FCSTD DOCUMENT  (FreeCAD 0.20R29410 (Git))
Label: SoLoNodesMay31_2023
License: All rights reserved
LicenseURL: http://en.wikipedia.org/wiki/All_rights_reserved
objects: Part::Feature×153, Sketcher::SketchObject×60, Part::Cylinder×60, Part::MultiFuse×52, Part::Cut×25, Part::Fillet×23, Part::Extrusion×20, Part::Loft×20, App::Part×19, Part::Sphere×6, Mesh::Feature×4, Part::Box×3, Part::Compound×2, Part::Cone×1
note: 425 computed .brp shape members not serialized (recipe doc carries the construction recipe); baked Part::Feature solids carry a one-line shape summary decoded from their .brp

FEATURE [Part::Feature] Part__Feature  label="PH Pan head screw M2x0.40 x 6"
  Placement = pos=(101.945,-83.8381,-1.82512) rot=(0,0,1;3.14159rad)
  shape: bbox 4.006 x 4.006 x 7.57 mm, 32 faces (baked)
FEATURE [Part::Feature] Part__Feature001  label="Part 8"
  Placement = pos=(178.445,24.1619,-39.4251) rot=(0,1,0;3.14159rad)
  shape: bbox 166 x 27.4 x 2 mm, 14 faces (baked)
FEATURE [Part::Feature] Part__Feature002  label="event gore PMF100320"
  Placement = pos=(79.1369,-76.58,11.5741) rot=(0,-1,0;0.037482rad)
  shape: bbox 2.468 x 15.31 x 15.29 mm, 4 faces (baked)
FEATURE [Part::Feature] Part__Feature003  label="event gore PMF100321"
  Placement = pos=(79.1369,-76.58,11.5741) rot=(0,-1,0;0.037482rad)
  shape: bbox 15.95 x 18.27 x 18.26 mm, 114 faces (baked)
FEATURE [Part::Feature] Part__Feature004  label="PH Pan head screw M2x0.40 x 007"
  Placement = pos=(101.945,24.1619,-1.82512) rot=(0,0,1;0rad)
  shape: bbox 4.006 x 4.006 x 7.57 mm, 32 faces (baked)
FEATURE [Part::Feature] Part__Feature005  label="WPB20-28-7_3D"
  Placement = pos=(178.445,24.1619,30.5749) rot=(0,0,1;0rad)
  shape: bbox 200.6 x 280.6 x 46.01 mm, 1035 faces (baked)
FEATURE [Part::Feature] Part__Feature006  label="PH Pan head screw M2x0.40 x 008"
  Placement = pos=(254.945,-83.8381,-1.82512) rot=(0,0,1;3.14159rad)
  shape: bbox 4.006 x 4.006 x 7.57 mm, 32 faces (baked)
FEATURE [Part::Feature] Part__Feature007  label="Cable Gland PG7-PG19 Lock Nut_PG13.5"
  Placement = pos=(223.445,-112.627,11.6686) rot=(1,0,0;0.037482rad)
  shape: bbox 29.02 x 6.449 x 29 mm, 29 faces (baked)
FEATURE [Part::Feature] Part__Feature008  label="Cable Gland PG7-PG19 Body_PG13.5"
  Placement = pos=(223.445,-118.923,11.4325) rot=(0,-0.01874,0.999824;3.14159rad)
  shape: bbox 25.06 x 36.36 x 23.18 mm, 156 faces (baked)
FEATURE [Part::Feature] Part__Feature009  label="Cable Gland PG7-PG19 Washer_PG13.5"
  Placement = pos=(223.445,-115.725,11.5524) rot=(0,-0.01874,0.999824;3.14159rad)
  shape: bbox 25 x 2.136 x 25.03 mm, 4 faces (baked)
FEATURE [Part::Feature] Part__Feature010  label="Cable Gland PG7-PG19 Gland Nut_PG13.5"
  Placement = pos=(223.445,-132.014,10.9416) rot=(0.825324,-0.010582,0.56456;3.17253rad)
  shape: bbox 25.82 x 20.19 x 25.8 mm, 50 faces (baked)
FEATURE [Part::Feature] Part__Feature011  label="Cable Gland PG7-PG19 Sleeve_PG13.5"
  Placement = pos=(223.445,-137.51,10.7355) rot=(0,-0.01874,0.999824;3.14159rad)
  shape: bbox 15.7 x 8.583 x 15.99 mm, 4 faces (baked)
FEATURE [App::Part] Cable_Gland_PG7_PG19__PG13_5__1_  label="Cable Gland PG7-PG19, PG13.5 <1>"
  Group = -> [Part__Feature007,Part__Feature008,Part__Feature009,Part__Feature010,Part__Feature011]
  Origin = -> Origin
FEATURE [Part::Feature] Part__Feature012  label="WPMB-M4-2"
  Placement = pos=(178.445,24.1619,-13.4251) rot=(0,1,0;3.14159rad)
  shape: bbox 91.99 x 91.99 x 12.05 mm, 899 faces (baked)
FEATURE [Part::Feature] Part__Feature013  label="Micro_USB_Plug v10"
  Placement = pos=(255.557,33.7719,7.31475) rot=(0.577351,0.577352,-0.577348;4.18879rad)
  shape: bbox 4.78 x 0.2 x 0.4672 mm, 14 faces (baked)
FEATURE [Part::Feature] Part__Feature014  label="Micro_USB_Plug_Connector"
  Placement = pos=(255.557,33.7719,7.31475) rot=(0.577351,0.577352,-0.577348;4.18879rad)
  shape: bbox 7.5 x 6.85 x 1.85 mm, 68 faces (baked)
FEATURE [Part::Feature] Part__Feature015  label="Micro_USB_Plug v011"
  Placement = pos=(255.557,33.7719,7.31475) rot=(0.577351,0.577352,-0.577348;4.18879rad)
  shape: bbox 4.78 x 0.2 x 0.4672 mm, 14 faces (baked)
FEATURE [Part::Feature] Part__Feature016  label="Micro_USB_Plug_Connector001"
  Placement = pos=(255.557,33.7719,7.31475) rot=(0.577351,0.577352,-0.577348;4.18879rad)
  shape: bbox 4.574 x 0.32 x 1.625 mm, 11 faces (baked)
FEATURE [Part::Feature] Part__Feature017  label="micro_usb_plug rt angle"
  Placement = pos=(255.557,33.7719,7.31475) rot=(0.577351,0.577352,-0.577348;4.18879rad)
  shape: bbox 12.25 x 19.75 x 7.006 mm, 151 faces (baked)
FEATURE [Part::Feature] Part__Feature018  label="Micro_USB_Plug v012"
  Placement = pos=(255.557,33.7719,7.31475) rot=(0.577351,0.577352,-0.577348;4.18879rad)
  shape: bbox 4.78 x 0.2 x 0.4672 mm, 14 faces (baked)
FEATURE [Part::Feature] Part__Feature019  label="Micro_USB_Plug v013"
  Placement = pos=(255.557,33.7719,7.31475) rot=(0.577351,0.577352,-0.577348;4.18879rad)
  shape: bbox 4.78 x 0.2 x 0.4672 mm, 14 faces (baked)
FEATURE [Part::Feature] Part__Feature020  label="Wire"
  Placement = pos=(255.557,33.7719,7.31475) rot=(0.577351,0.577352,-0.577348;4.18879rad)
  shape: bbox 3.2 x 9.5 x 3.2 mm, 3 faces (baked)
FEATURE [Part::Feature] Part__Feature021  label="Micro_USB_Plug_Connector002"
  Placement = pos=(255.557,33.7719,7.31475) rot=(0.577351,0.577352,-0.577348;4.18879rad)
  shape: bbox 4.7 x 0.32 x 1.625 mm, 11 faces (baked)
FEATURE [Part::Feature] Part__Feature022  label="Micro_USB_Plug v014"
  Placement = pos=(255.557,33.7719,7.31475) rot=(0.577351,0.577352,-0.577348;4.18879rad)
  shape: bbox 4.78 x 0.2 x 0.4672 mm, 14 faces (baked)
FEATURE [Part::Feature] Part__Feature023  label="Micro_USB_Plug_Connector003"
  Placement = pos=(255.557,33.7719,7.31475) rot=(0.577351,0.577352,-0.577348;4.18879rad)
  shape: bbox 7.5 x 6.35 x 1.35 mm, 54 faces (baked)
FEATURE [Part::Feature] Part__Feature024  label="2_C_3_4_6_1_1"
  Placement = pos=(205.099,-19.2281,8.57488) rot=(-1,-3e-06,-3e-06;1.57079rad)
  shape: bbox 73.52 x 148.2 x 33.63 mm, 876 faces (baked)
FEATURE [Part::Feature] Part__Feature025  label="2_BAT_3_4_6_1_1"
  Placement = pos=(205.099,-19.2281,8.57488) rot=(-1,-3e-06,-3e-06;1.57079rad)
  shape: bbox 14.36 x 15.32 x 64.97 mm, 83 faces (baked)
FEATURE [Part::Feature] Part__Feature026  label="2_B_3_4_6_1_1"
  Placement = pos=(205.099,-19.2281,8.57488) rot=(-1,-3e-06,-3e-06;1.57079rad)
  shape: bbox 78.1 x 152 x 64.86 mm, 1086 faces (baked)
FEATURE [Part::Feature] Part__Feature027  label="2_A_3_4_6_2_1"
  Placement = pos=(205.099,-19.2281,8.57488) rot=(-1,-3e-06,-3e-06;1.57079rad)
  shape: bbox 73.51 x 148.2 x 58.23 mm, 268 faces (baked)
FEATURE [App::Part] V75_ASM__1_  label="V75 ASM <1>"
  Group = -> [Part__Feature013,Part__Feature014,Part__Feature015,Part__Feature016,Part__Feature017,Part__Feature018,Part__Feature019,Part__Feature020,Part__Feature021,Part__Feature022,Part__Feature023,Part__Feature024,Part__Feature025,Part__Feature026,Part__Feature027]
  Origin = -> Origin001
  Placement = pos=(6,15.97,20) rot=(0,0,1;0rad)
FEATURE [Part::Feature] Part__Feature028  label="PH Pan head screw M2x0.40 x 009"
  Placement = pos=(254.945,24.1619,-1.82512) rot=(0,0,1;0rad)
  shape: bbox 4.006 x 4.006 x 7.57 mm, 32 faces (baked)
FEATURE [Part::Feature] Part__Feature029  label="Part 009"
  Placement = pos=(178.445,-83.8381,-39.4251) rot=(1,0,0;3.14159rad)
  shape: bbox 166 x 27.4 x 2 mm, 14 faces (baked)
FEATURE [Part::Feature] Part__Feature030  label="WPC20-28_3D"
  Placement = pos=(178.435,24.1794,31.5749) rot=(0,0,1;0rad)
  shape: bbox 201.1 x 281.1 x 21.57 mm, 1217 faces (baked)
FEATURE [Part::Feature] Part__Feature031  label="Cable Gland PG7-PG19 Sleeve_PG9"
  Placement = pos=(133.445,-133.413,10.8891) rot=(0,-0.01874,0.999824;3.14159rad)
  shape: bbox 11 x 8.207 x 11.28 mm, 4 faces (baked)
FEATURE [Part::Feature] Part__Feature032  label="Cable Gland PG7-PG19 Washer_PG9"
  Placement = pos=(133.445,-115.725,11.5524) rot=(0,-0.01874,0.999824;3.14159rad)
  shape: bbox 19.7 x 1.937 x 19.73 mm, 4 faces (baked)
FEATURE [Part::Feature] Part__Feature033  label="Cable Gland PG7-PG19 Lock Nut_PG9"
  Placement = pos=(133.445,-112.627,11.6686) rot=(1,0,0;0.037482rad)
  shape: bbox 24.34 x 6.322 x 24.32 mm, 29 faces (baked)
FEATURE [Part::Feature] Part__Feature034  label="Cable Gland PG7-PG19 Body_PG9"
  Placement = pos=(133.445,-118.823,11.4362) rot=(0,-0.01874,0.999824;3.14159rad)
  shape: bbox 19.4 x 32.49 x 17.68 mm, 129 faces (baked)
FEATURE [Part::Feature] Part__Feature035  label="Cable Gland PG7-PG19 Gland Nut_PG9"
  Placement = pos=(133.445,-130.065,11.0147) rot=(0.825324,-0.010582,0.56456;3.17253rad)
  shape: bbox 20.81 x 16.04 x 20.8 mm, 48 faces (baked)
FEATURE [App::Part] Cable_Gland_PG7_PG19__PG9__1_  label="Cable Gland PG7-PG19, PG9 <1>"
  Group = -> [Part__Feature031,Part__Feature032,Part__Feature033,Part__Feature034,Part__Feature035]
  Origin = -> Origin002
FEATURE [App::Part] E305__20x28x7cm_  label="box"
  Group = -> [Part__Feature,Part__Feature001,Part__Feature002,Part__Feature003,Part__Feature004,Part__Feature005,Part__Feature006,Cable_Gland_PG7_PG19__PG13_5__1_,Part__Feature012,V75_ASM__1_,Part__Feature028,Part__Feature029,Part__Feature030,Cable_Gland_PG7_PG19__PG9__1_]
  Origin = -> Origin003
  Placement = pos=(175.533,-124.11,-130.152) rot=(0,-0.939693,-0.34202;3.14159rad)
FEATURE [Part::Feature] Part__Feature036  label="id2"
  shape: bbox 274 x 229.5 x 2.5 mm, 53 faces (baked)
FEATURE [Part::Feature] Part__Feature037  label="id5"
  shape: bbox 251.2 x 70.58 x 83.44 mm, 48 faces (baked)
FEATURE [Part::Feature] Part__Feature038  label="id8"
  shape: bbox 253.5 x 2.737 x 2.883 mm, 6 faces (baked)
FEATURE [Part::MultiFuse] Fusion  label="solarPanelMount"
  Placement = pos=(0,0,0) rot=(1,0,0;0.698132rad)
  Shapes = -> [Part__Feature036,Part__Feature037,Part__Feature038]
FEATURE [Part::Feature] Part__Feature039  label="Part 2"
  Placement = pos=(-0.595807,44.562,74.9733) rot=(1,0,0;3.14159rad)
  shape: bbox 272 x 434 x 1.1 mm, 24 faces (baked)
FEATURE [Part::Feature] Part__Feature041  label="id16"
  Placement = pos=(-0.595807,44.562,69.8733) rot=(0,0,1;0rad)
  shape: bbox 4 x 8.79 x 2 mm, 10 faces (baked)
FEATURE [Part::Feature] Part__Feature042  label="id21"
  Placement = pos=(-0.595807,44.562,69.8733) rot=(0,0,1;0rad)
  shape: bbox 125 x 42.28 x 0.1 mm, 8 faces (baked)
FEATURE [Part::Feature] Part__Feature043  label="id26"
  Placement = pos=(-0.595807,44.562,69.8733) rot=(0,0,1;0rad)
  shape: bbox 125 x 42.28 x 0.1 mm, 8 faces (baked)
FEATURE [Part::Feature] Part__Feature044  label="id31"
  Placement = pos=(-0.595807,44.562,69.8733) rot=(0,0,1;0rad)
  shape: bbox 4 x 8.79 x 2 mm, 10 faces (baked)
FEATURE [Part::Feature] Part__Feature045  label="id36"
  Placement = pos=(-0.595807,44.562,69.8733) rot=(0,0,1;0rad)
  shape: bbox 125 x 42.28 x 0.1 mm, 8 faces (baked)
FEATURE [Part::Feature] Part__Feature046  label="id41"
  Placement = pos=(-0.595807,44.562,69.8733) rot=(0,0,1;0rad)
  shape: bbox 4 x 4 x 2 mm, 4 faces (baked)
FEATURE [Part::Feature] Part__Feature047  label="id46"
  Placement = pos=(-0.595807,44.562,69.8733) rot=(0,0,1;0rad)
  shape: bbox 4 x 4 x 2 mm, 4 faces (baked)
FEATURE [Part::Feature] Part__Feature048  label="id51"
  Placement = pos=(-0.595807,44.562,69.8733) rot=(0,0,1;0rad)
  shape: bbox 125 x 42.28 x 0.1 mm, 8 faces (baked)
FEATURE [Part::Feature] Part__Feature049  label="id56"
  Placement = pos=(-0.595807,44.562,69.8733) rot=(0,0,1;0rad)
  shape: bbox 125 x 42.28 x 0.1 mm, 8 faces (baked)
FEATURE [Part::Feature] Part__Feature050  label="id61"
  Placement = pos=(-0.595807,44.562,69.8733) rot=(0,0,1;0rad)
  shape: bbox 4 x 4 x 2 mm, 4 faces (baked)
FEATURE [Part::Feature] Part__Feature051  label="id66"
  Placement = pos=(-0.595807,44.562,69.8733) rot=(0,0,1;0rad)
  shape: bbox 125 x 42.28 x 0.1 mm, 8 faces (baked)
FEATURE [Part::Feature] Part__Feature052  label="id71"
  Placement = pos=(-0.595807,44.562,69.8733) rot=(0,0,1;0rad)
  shape: bbox 125 x 40.44 x 0.1 mm, 6 faces (baked)
FEATURE [Part::Feature] Part__Feature053  label="id76"
  Placement = pos=(-0.595807,44.562,69.8733) rot=(0,0,1;0rad)
  shape: bbox 125 x 40.44 x 0.1 mm, 6 faces (baked)
FEATURE [Part::Feature] Part__Feature054  label="id81"
  Placement = pos=(-0.595807,44.562,69.8733) rot=(0,0,1;0rad)
  shape: bbox 125 x 42.28 x 0.1 mm, 8 faces (baked)
FEATURE [Part::Feature] Part__Feature055  label="id86"
  Placement = pos=(-0.595807,44.562,69.8733) rot=(0,0,1;0rad)
  shape: bbox 125 x 42.28 x 0.1 mm, 8 faces (baked)
FEATURE [Part::Feature] Part__Feature056  label="id91"
  Placement = pos=(-0.595807,44.562,69.8733) rot=(0,0,1;0rad)
  shape: bbox 125 x 42.28 x 0.1 mm, 8 faces (baked)
FEATURE [Part::Feature] Part__Feature057  label="id96"
  Placement = pos=(-0.595807,44.562,69.8733) rot=(0,0,1;0rad)
  shape: bbox 272 x 434 x 2 mm, 24 faces (baked)
FEATURE [Part::Feature] Part__Feature058  label="id101"
  Placement = pos=(-0.595807,44.562,69.8733) rot=(0,0,1;0rad)
  shape: bbox 125 x 42.28 x 0.1 mm, 8 faces (baked)
FEATURE [Part::Feature] Part__Feature059  label="id106"
  Placement = pos=(-0.595807,44.562,69.8733) rot=(0,0,1;0rad)
  shape: bbox 125 x 42.28 x 0.1 mm, 8 faces (baked)
FEATURE [Part::Feature] Part__Feature060  label="id111"
  Placement = pos=(-0.595807,44.562,69.8733) rot=(0,0,1;0rad)
  shape: bbox 125 x 42.28 x 0.1 mm, 8 faces (baked)
FEATURE [Part::Feature] Part__Feature061  label="id116"
  Placement = pos=(-0.595807,44.562,69.8733) rot=(0,0,1;0rad)
  shape: bbox 4 x 4 x 2 mm, 4 faces (baked)
FEATURE [Part::Feature] Part__Feature062  label="id121"
  Placement = pos=(-0.595807,44.562,69.8733) rot=(0,0,1;0rad)
  shape: bbox 4 x 4 x 2 mm, 4 faces (baked)
FEATURE [Part::Feature] Part__Feature063  label="id126"
  Placement = pos=(-0.595807,44.562,69.8733) rot=(0,0,1;0rad)
  shape: bbox 125 x 42.28 x 0.1 mm, 8 faces (baked)
FEATURE [Part::Feature] Part__Feature064  label="id131"
  Placement = pos=(-0.595807,44.562,69.8733) rot=(0,0,1;0rad)
  shape: bbox 4 x 4 x 2 mm, 4 faces (baked)
FEATURE [Part::Feature] Part__Feature065  label="id136"
  Placement = pos=(-0.595807,44.562,69.8733) rot=(0,0,1;0rad)
  shape: bbox 125 x 40.44 x 0.1 mm, 6 faces (baked)
FEATURE [Part::Feature] Part__Feature066  label="id141"
  Placement = pos=(-0.595807,44.562,69.8733) rot=(0,0,1;0rad)
  shape: bbox 274 x 436 x 2 mm, 18 faces (baked)
FEATURE [Part::Feature] Part__Feature067  label="id146"
  Placement = pos=(-0.595807,44.562,69.8733) rot=(0,0,1;0rad)
  shape: bbox 125 x 42.28 x 0.1 mm, 8 faces (baked)
FEATURE [Part::Feature] Part__Feature068  label="id151"
  Placement = pos=(-0.595807,44.562,69.8733) rot=(0,0,1;0rad)
  shape: bbox 125 x 42.28 x 0.1 mm, 8 faces (baked)
FEATURE [Part::Feature] Part__Feature069  label="id156"
  Placement = pos=(-0.595807,44.562,69.8733) rot=(0,0,1;0rad)
  shape: bbox 125 x 42.28 x 0.1 mm, 8 faces (baked)
FEATURE [Part::Feature] Part__Feature070  label="id161"
  Placement = pos=(-0.595807,44.562,69.8733) rot=(0,0,1;0rad)
  shape: bbox 125 x 40.44 x 0.1 mm, 6 faces (baked)
FEATURE [Part::Feature] Part__Feature076  label="Part 1"
  Placement = pos=(-0.595807,44.562,74.9733) rot=(1,0,0;3.14159rad)
  shape: bbox 274 x 436 x 1.1 mm, 18 faces (baked)
FEATURE [Part::Feature] Part__Feature077  label="JBox - 30 mm"
  Placement = pos=(-50.5959,-43.7114,69.8733) rot=(0,1,0;3.14159rad)
  shape: bbox 30.01 x 30.09 x 5.866 mm, 175 faces (baked)
FEATURE [App::Part] P120  label="solarPanel"
  Group = -> [Part__Feature039,Part__Feature041,Part__Feature042,Part__Feature043,Part__Feature044,Part__Feature045,Part__Feature046,Part__Feature047,Part__Feature048,Part__Feature049,Part__Feature050,Part__Feature051,Part__Feature052,Part__Feature053,Part__Feature054,Part__Feature055,Part__Feature056,Part__Feature057,Part__Feature058,Part__Feature059,Part__Feature060,Part__Feature061,Part__Feature062,+10 more]
  Origin = -> Origin004
  Placement = pos=(0.6,-120,-180) rot=(1,0,0;0.698132rad)
FEATURE [Part::Feature] Part__Feature078  label="Open CASCADE STEP translator 7.4 2.1.1"
  shape: bbox 8.3 x 1.9 x 1 mm, 10 faces, 0 solids (baked)
FEATURE [Part::Feature] Part__Feature079  label="Open CASCADE STEP translator 7.4 2.1.2"
  shape: bbox 12.5 x 10 x 1.5 mm, 6 faces, 0 solids (baked)
FEATURE [Part::Feature] Part__Feature080  label="Open CASCADE STEP translator 7.4 2.1.3"
  shape: bbox 12.5 x 10 x 1.5 mm, 6 faces, 0 solids (baked)
FEATURE [Part::Feature] Part__Feature081  label="Open CASCADE STEP translator 7.4 2.1.4"
  shape: bbox 12.5 x 10 x 1.5 mm, 6 faces, 0 solids (baked)
FEATURE [Part::Feature] Part__Feature082  label="Open CASCADE STEP translator 7.4 2.1.5"
  shape: bbox 12.5 x 10 x 1.5 mm, 6 faces, 0 solids (baked)
FEATURE [Part::Feature] Part__Feature083  label="Open CASCADE STEP translator 7.4 2.1.6"
  shape: bbox 89.5 x 57.1 x 20.65 mm, 2741 faces, 0 solids (baked)
FEATURE [App::Part] Open_CASCADE_STEP_translator_7_4_2_1  label="Open CASCADE STEP translator 7.4 2.1"
  Group = -> [Part__Feature078,Part__Feature079,Part__Feature080,Part__Feature081,Part__Feature082,Part__Feature083]
  Origin = -> Origin005
FEATURE [Part::Feature] Part__Feature084  label="m312mm"
  Placement = pos=(63.5,-7,61.5) rot=(0,0.707107,0.707107;3.14159rad)
  shape: bbox 6.201 x 15.54 x 6.201 mm, 70 faces (baked)
FEATURE [Part::Feature] Part__Feature085  label="m312mm001"
  Placement = pos=(14.5,-7,61.5) rot=(-1,0,0;1.5708rad)
  shape: bbox 6.201 x 15.54 x 6.201 mm, 70 faces (baked)
FEATURE [Part::MultiFuse] Fusion003
  Shapes = -> [Part__Feature085,Part__Feature084]
FEATURE [Part::Feature] Part__Feature086  label="m312mm002"
  Placement = pos=(14.5,-7,61.5) rot=(-1,0,0;1.5708rad)
  shape: bbox 6.201 x 15.54 x 6.201 mm, 70 faces (baked)
FEATURE [Part::Feature] Part__Feature087  label="m312mm003"
  Placement = pos=(63.5,-7,61.5) rot=(0,0.707107,0.707107;3.14159rad)
  shape: bbox 6.201 x 15.54 x 6.201 mm, 70 faces (baked)
FEATURE [Part::MultiFuse] Fusion004
  Placement = pos=(0,0,-58) rot=(0,0,1;0rad)
  Shapes = -> [Part__Feature086,Part__Feature087]
FEATURE [Part::MultiFuse] Fusion005  label="m3s"
  Placement = pos=(0.1,-1,0) rot=(0,0,1;0rad)
  Shapes = -> [Fusion004,Fusion003]
FEATURE [App::Part] Open_CASCADE_STEP_translator_7_4_2  label="C4"
  Group = -> [Open_CASCADE_STEP_translator_7_4_2_1,Part__Feature084,Part__Feature085,Fusion003,Part__Feature086,Part__Feature087,Fusion004,Fusion005]
  Origin = -> Origin006
  Placement = pos=(-15,-5,-224) rot=(0.57735,-0.57735,0.57735;2.0944rad)
FEATURE [Part::Feature] Part__Feature088  label="MainBoard"
  shape: bbox 50 x 23 x 1.8 mm, 90 faces (baked)
FEATURE [Part::Feature] Part__Feature089  label="USB Type C Port (SMD Type)"
  Placement = pos=(-18.7,0.12,3.4) rot=(0.707107,-0.707107,0;3.14159rad)
  shape: bbox 7.901 x 8.941 x 4.201 mm, 394 faces, 24 solids (baked)
FEATURE [Part::Feature] Part__Feature090  label="LoRaSTM32Chip"
  Placement = pos=(8.97,0,1.8) rot=(0,0,1;0rad)
  shape: bbox 12 x 12 x 2.5 mm, 68 faces (baked)
FEATURE [Part::Feature] Part__Feature091  label="E10_433M_SMA122"
  Placement = pos=(13,-2.15,1.4) rot=(0,0,1;0rad)
  shape: bbox 11.33 x 1.55 x 1.55 mm, 34 faces (baked)
FEATURE [Part::Feature] Part__Feature092  label="E10_433M_SMA123"
  Placement = pos=(13,-2.15,1.4) rot=(0,0,1;0rad)
  shape: bbox 13.33 x 6.493 x 6.493 mm, 59 faces (baked)
FEATURE [Part::Feature] Part__Feature093  label="CP2012"
  Placement = pos=(-8.75,0.13,1.82) rot=(0,0,1;0rad)
  shape: bbox 4 x 4 x 0.7 mm, 6 faces (baked)
FEATURE [Part::Feature] Part__Feature094  label="u.Fl Antenna Connector - 523-A-1JB"
  Placement = pos=(24.2,5.8,1.8) rot=(0,0.707107,0.707107;3.14159rad)
  shape: bbox 3.1 x 3 x 1.25 mm, 82 faces, 5 solids (baked)
FEATURE [Part::Feature] Part__Feature095  label="Top Traces"
  shape: bbox 49.4 x 23 x 0.02 mm, 7906 faces, 207 solids (baked)
FEATURE [App::Part] LoRa_E5_Mini  label="LoRa-E5-Mini"
  Group = -> [Part__Feature088,Part__Feature089,Part__Feature090,Part__Feature091,Part__Feature092,Part__Feature093,Part__Feature094,Part__Feature095]
  Origin = -> Origin007
  Placement = pos=(-44,0,-220) rot=(0.57735,0.57735,-0.57735;2.0944rad)
FEATURE [Part::Feature] Part__Feature096  label="nanoSupport001"
  Placement = pos=(-30,0,-97) rot=(0.57735,-0.57735,0.57735;2.0944rad)
  shape: bbox 56 x 30 x 43 mm, 8 faces (baked)
FEATURE [Sketcher::SketchObject] Sketch
  FullyConstrained = true
  MapMode = 3
  Placement = pos=(178.445,24.1619,-13.4251) rot=(0,0.707107,-0.707107;3.14159rad)
  Support = -> [Part__Feature012]
  sketch-geometry (32):
    g0: LineSegment StartX=99 StartY=265 StartZ=0 EndX=261 EndY=265 EndZ=0
    g1: LineSegment StartX=261 StartY=265 StartZ=0 EndX=261 EndY=40 EndZ=0
    g2: LineSegment StartX=261 StartY=40 StartZ=0 EndX=99 EndY=40 EndZ=0
    g3: LineSegment StartX=99 StartY=40 StartZ=0 EndX=99 EndY=265 EndZ=0
    g4: Circle CenterX=103.5 CenterY=260.4 CenterZ=0 NormalX=0 NormalY=0 NormalZ=1 AngleXU=0 Radius=1.25
    g5: Circle CenterX=256.5 CenterY=260.4 CenterZ=0 NormalX=0 NormalY=0 NormalZ=1 AngleXU=0 Radius=1.25
    g6: Circle CenterX=103.5 CenterY=152.4 CenterZ=0 NormalX=0 NormalY=0 NormalZ=1 AngleXU=0 Radius=1.25
    g7: Circle CenterX=103.5 CenterY=44.4 CenterZ=0 NormalX=0 NormalY=0 NormalZ=1 AngleXU=0 Radius=1.25
    g8: Circle CenterX=256.5 CenterY=44.4 CenterZ=0 NormalX=0 NormalY=0 NormalZ=1 AngleXU=0 Radius=1.25
    g9: Circle CenterX=256.5 CenterY=152.4 CenterZ=0 NormalX=0 NormalY=0 NormalZ=1 AngleXU=0 Radius=1.25
    g10: Circle CenterX=213.46 CenterY=229.1 CenterZ=0 NormalX=0 NormalY=0 NormalZ=1 AngleXU=0 Radius=1.25
    g11: Circle CenterX=231.46 CenterY=229.1 CenterZ=0 NormalX=0 NormalY=0 NormalZ=1 AngleXU=0 Radius=1.25
    g12: Circle CenterX=213.46 CenterY=194.1 CenterZ=0 NormalX=0 NormalY=0 NormalZ=1 AngleXU=0 Radius=1.25
    g13: Circle CenterX=231.46 CenterY=194.1 CenterZ=0 NormalX=0 NormalY=0 NormalZ=1 AngleXU=0 Radius=1.25
    g14: Circle CenterX=245.95 CenterY=207.08 CenterZ=0 NormalX=0 NormalY=0 NormalZ=1 AngleXU=0 Radius=1.625
    g15: Circle CenterX=196.95 CenterY=207.08 CenterZ=0 NormalX=0 NormalY=0 NormalZ=1 AngleXU=0 Radius=1.625
    g16: Circle CenterX=245.95 CenterY=149.08 CenterZ=0 NormalX=0 NormalY=0 NormalZ=1 AngleXU=0 Radius=1.625
    g17: Circle CenterX=196.95 CenterY=149.08 CenterZ=0 NormalX=0 NormalY=0 NormalZ=1 AngleXU=0 Radius=1.625
    g18: Circle CenterX=208.2 CenterY=101.58 CenterZ=0 NormalX=0 NormalY=0 NormalZ=1 AngleXU=0 Radius=1.25
    g19: Circle CenterX=208.2 CenterY=94.58 CenterZ=0 NormalX=0 NormalY=0 NormalZ=1 AngleXU=0 Radius=1.25
    g20: Circle CenterX=238.2 CenterY=101.58 CenterZ=0 NormalX=0 NormalY=0 NormalZ=1 AngleXU=0 Radius=1.25
    g21: Circle CenterX=246.2 CenterY=62.1 CenterZ=0 NormalX=0 NormalY=0 NormalZ=1 AngleXU=0 Radius=1.625
    g22: Circle CenterX=200.7 CenterY=62.1 CenterZ=0 NormalX=0 NormalY=0 NormalZ=1 AngleXU=0 Radius=1.625
    g23: Circle CenterX=238.2 CenterY=94.58 CenterZ=0 NormalX=0 NormalY=0 NormalZ=1 AngleXU=0 Radius=1.25
    g24: Circle CenterX=138 CenterY=105 CenterZ=0 NormalX=0 NormalY=0 NormalZ=1 AngleXU=0 Radius=5
    g25: Circle CenterX=156.7 CenterY=105 CenterZ=0 NormalX=0 NormalY=0 NormalZ=1 AngleXU=0 Radius=5
    g26: Circle CenterX=138 CenterY=255 CenterZ=0 NormalX=0 NormalY=0 NormalZ=1 AngleXU=0 Radius=5
    g27: Circle CenterX=156.7 CenterY=255 CenterZ=0 NormalX=0 NormalY=0 NormalZ=1 AngleXU=0 Radius=5
    g28: Circle CenterX=110 CenterY=220 CenterZ=0 NormalX=0 NormalY=0 NormalZ=1 AngleXU=0 Radius=5
    g29: Circle CenterX=184.8 CenterY=220 CenterZ=0 NormalX=0 NormalY=0 NormalZ=1 AngleXU=0 Radius=5
    g30: Circle CenterX=110 CenterY=170 CenterZ=0 NormalX=0 NormalY=0 NormalZ=1 AngleXU=0 Radius=5
    g31: Circle CenterX=184.8 CenterY=170 CenterZ=0 NormalX=0 NormalY=0 NormalZ=1 AngleXU=0 Radius=5
  constraints (86):
    c: Coincident(g0,g1)
    c: Coincident(g1,g2)
    c: Coincident(g2,g3)
    c: Coincident(g3,g0)
    c: Horizontal(g0)
    c: Horizontal(g2)
    c: Vertical(g1)
    c: Vertical(g3)
    c: DistanceX(g2) = 99
    c: DistanceX(g1) = 261
    c: DistanceY(g2) = 40
    c: DistanceY(g0) = 265
    c: Equal(g18,g19)
    c: Equal(g18,g20)
    c: Equal(g18,g23)
    c: Equal(g18,g9)
    c: Equal(g18, g4-g8) x5
    c: Equal(g18, g10-g13) x4
    c: Radius(g18) = 1.25
    c: DistanceX(g7) = 103.5
    c: DistanceY(g7) = 44.4
    c: DistanceX(g7,g6) = 0
    c: DistanceX(g4,g6) = 0
    c: DistanceX(g7,g8) = 153
    c: DistanceY(g7,g8) = 0
    c: DistanceY(g6,g9) = 0
    c: DistanceY(g5,g4) = 0
    c: DistanceX(g8,g9) = 0
    c: DistanceX(g9,g5) = 0
    c: DistanceX(g17) = 196.95
    c: DistanceY(g17) = 149.08
    c: Equal(g14,g16)
    c: Equal(g14,g17)
    c: Equal(g14,g15)
    c: Diameter(g14) = 3.25
    c: DistanceX(g17,g16) = 49
    c: DistanceY(g17,g16) = 0
    c: DistanceY(g17,g15) = 58
    c: DistanceX(g17,g15) = 0
    c: DistanceY(g14,g15) = 0
    c: DistanceX(g14,g16) = 0
    c: DistanceX(g12) = 213.46
    c: DistanceY(g12) = 194.1
    c: DistanceY(g13,g12) = 0
    c: DistanceX(g12,g13) = 18
    c: DistanceX(g10,g12) = 0
    c: DistanceX(g11,g13) = 0
    c: DistanceY(g12,g10) = 35
    c: DistanceY(g11,g10) = 0
    c: Equal(g24,g25)
    c: Equal(g24,g30)
    c: Equal(g24,g31)
    c: Equal(g24, g26-g29) x4
    c: Diameter(g24) = 10
    c: DistanceY(g24) = 105
    c: DistanceY(g25,g24) = 0
    c: DistanceX(g24) = 138
    c: DistanceX(g24,g25) = 18.7
    c: DistanceY(g24,g26) = 150
    c: DistanceX(g26,g24) = 0
    c: DistanceX(g27,g25) = 0
    c: DistanceY(g26,g27) = 0
    c: DistanceX(g30) = 110
    c: DistanceY(g30) = 170
    c: DistanceY(g30,g31) = 0
    c: DistanceX(g30,g31) = 74.8
    c: DistanceY(g30,g28) = 50
    c: DistanceY(g28,g29) = 0
    c: DistanceX(g28,g30) = 0
    c: DistanceX(g31,g29) = 0
    c: DistanceY(g7,g4) = 216
    c: DistanceX(g7,g22) = 97.2
    c: DistanceY(g22,g21) = 0
    c: DistanceX(g22,g21) = 45.5
    c: DistanceY(g22) = 62.1
    c: DistanceX(g7,g19) = 104.7
    c: DistanceY(g19) = 94.58
    c: DistanceX(g18,g19) = 0
    c: DistanceY(g19,g18) = 7
    c: DistanceX(g19,g23) = 30
    c: DistanceY(g23,g19) = 0
    c: DistanceX(g23,g20) = 0
    c: DistanceY(g18,g20) = 0
    c: Equal(g22,g21)
    c: Diameter(g22) = 3.25
    c: DistanceY(g7,g6) = 108
FEATURE [Part::Box] Box007  label="Cube007"
  AttacherType = Attacher::AttachEngine3D
  Height = 17
  Length = 36.5
  Width = 3
FEATURE [Part::Cylinder] Cylinder012  label="m2s"
  Angle = 360
  AttacherType = Attacher::AttachEngine3D
  FirstAngle = 0
  Height = 10
  Placement = pos=(0,0,0) rot=(1,0,0;1.5708rad)
  Radius = 1.2
  SecondAngle = 0
FEATURE [Part::Cylinder] Cylinder014  label="m2s001"
  Angle = 360
  AttacherType = Attacher::AttachEngine3D
  FirstAngle = 0
  Height = 10
  Placement = pos=(30,0,0) rot=(1,0,0;1.5708rad)
  Radius = 1.2
  SecondAngle = 0
FEATURE [Part::Cylinder] Cylinder015  label="m2s002"
  Angle = 360
  AttacherType = Attacher::AttachEngine3D
  FirstAngle = 0
  Height = 10
  Placement = pos=(0,0,0) rot=(1,0,0;1.5708rad)
  Radius = 1.2
  SecondAngle = 0
FEATURE [Part::Cylinder] Cylinder016  label="m2s003"
  Angle = 360
  AttacherType = Attacher::AttachEngine3D
  FirstAngle = 0
  Height = 10
  Placement = pos=(30,0,0) rot=(1,0,0;1.5708rad)
  Radius = 1.2
  SecondAngle = 0
FEATURE [Part::MultiFuse] Fusion017
  Placement = pos=(3.25,0,0) rot=(0,0,1;0rad)
  Shapes = -> [Cylinder014,Cylinder012]
FEATURE [Part::MultiFuse] Fusion018
  Placement = pos=(3.25,0,7) rot=(0,0,1;0rad)
  Shapes = -> [Cylinder016,Cylinder015]
FEATURE [Part::MultiFuse] Fusion019
  Placement = pos=(0,3,5) rot=(0,0,1;0rad)
  Shapes = -> [Fusion017,Fusion018]
FEATURE [Part::Cut] Cut003
  Base = -> Box007
  Tool = -> Fusion019
FEATURE [Part::Fillet] Fillet008  label="converterSupport"
  Base = -> Cut003
  Edges = 4 edges r=2: [Edge2,Edge4,Edge13,Edge20]
  Placement = pos=(-63,5,-120) rot=(0,0,1;0rad)
FEATURE [Part::Extrusion] Extrude
  Base = -> Sketch
  Dir = (0,-1,2e-16)
  DirMode = 2
  FaceMakerClass = Part::FaceMakerBullseye
  LengthFwd = 4
  LengthRev = 0
  Solid = true
  Symmetric = false
FEATURE [Sketcher::SketchObject] Sketch001
  FullyConstrained = true
  MapMode = 3
  Placement = pos=(178.445,24.1619,-13.4251) rot=(0,0.707107,-0.707107;3.14159rad)
  sketch-geometry (32):
    g0: LineSegment StartX=99 StartY=265 StartZ=0 EndX=261 EndY=265 EndZ=0
    g1: LineSegment StartX=261 StartY=265 StartZ=0 EndX=261 EndY=40 EndZ=0
    g2: LineSegment StartX=261 StartY=40 StartZ=0 EndX=99 EndY=40 EndZ=0
    g3: LineSegment StartX=99 StartY=40 StartZ=0 EndX=99 EndY=265 EndZ=0
    g4: Circle CenterX=103.5 CenterY=260.4 CenterZ=0 NormalX=0 NormalY=0 NormalZ=1 AngleXU=0 Radius=1.25
    g5: Circle CenterX=256.5 CenterY=260.4 CenterZ=0 NormalX=0 NormalY=0 NormalZ=1 AngleXU=0 Radius=1.25
    g6: Circle CenterX=103.5 CenterY=152.4 CenterZ=0 NormalX=0 NormalY=0 NormalZ=1 AngleXU=0 Radius=1.25
    g7: Circle CenterX=103.5 CenterY=44.4 CenterZ=0 NormalX=0 NormalY=0 NormalZ=1 AngleXU=0 Radius=1.25
    g8: Circle CenterX=256.5 CenterY=44.4 CenterZ=0 NormalX=0 NormalY=0 NormalZ=1 AngleXU=0 Radius=1.25
    g9: Circle CenterX=256.5 CenterY=152.4 CenterZ=0 NormalX=0 NormalY=0 NormalZ=1 AngleXU=0 Radius=1.25
    g10: Circle CenterX=213.46 CenterY=229.1 CenterZ=0 NormalX=0 NormalY=0 NormalZ=1 AngleXU=0 Radius=1.25
    g11: Circle CenterX=231.46 CenterY=229.1 CenterZ=0 NormalX=0 NormalY=0 NormalZ=1 AngleXU=0 Radius=1.25
    g12: Circle CenterX=213.46 CenterY=194.1 CenterZ=0 NormalX=0 NormalY=0 NormalZ=1 AngleXU=0 Radius=1.25
    g13: Circle CenterX=231.46 CenterY=194.1 CenterZ=0 NormalX=0 NormalY=0 NormalZ=1 AngleXU=0 Radius=1.25
    g14: Circle CenterX=245.95 CenterY=207.08 CenterZ=0 NormalX=0 NormalY=0 NormalZ=1 AngleXU=0 Radius=1.625
    g15: Circle CenterX=196.95 CenterY=207.08 CenterZ=0 NormalX=0 NormalY=0 NormalZ=1 AngleXU=0 Radius=1.625
    g16: Circle CenterX=245.95 CenterY=149.08 CenterZ=0 NormalX=0 NormalY=0 NormalZ=1 AngleXU=0 Radius=1.625
    g17: Circle CenterX=196.95 CenterY=149.08 CenterZ=0 NormalX=0 NormalY=0 NormalZ=1 AngleXU=0 Radius=1.625
    g18: Circle CenterX=208.2 CenterY=101.58 CenterZ=0 NormalX=0 NormalY=0 NormalZ=1 AngleXU=0 Radius=1.25
    g19: Circle CenterX=208.2 CenterY=94.58 CenterZ=0 NormalX=0 NormalY=0 NormalZ=1 AngleXU=0 Radius=1.25
    g20: Circle CenterX=238.2 CenterY=101.58 CenterZ=0 NormalX=0 NormalY=0 NormalZ=1 AngleXU=0 Radius=1.25
    g21: Circle CenterX=246.2 CenterY=62.1 CenterZ=0 NormalX=0 NormalY=0 NormalZ=1 AngleXU=0 Radius=1.625
    g22: Circle CenterX=200.7 CenterY=62.1 CenterZ=0 NormalX=0 NormalY=0 NormalZ=1 AngleXU=0 Radius=1.625
    g23: Circle CenterX=238.2 CenterY=94.58 CenterZ=0 NormalX=0 NormalY=0 NormalZ=1 AngleXU=0 Radius=1.25
    g24: Circle CenterX=138 CenterY=105 CenterZ=0 NormalX=0 NormalY=0 NormalZ=1 AngleXU=0 Radius=5
    g25: Circle CenterX=156.7 CenterY=105 CenterZ=0 NormalX=0 NormalY=0 NormalZ=1 AngleXU=0 Radius=5
    g26: Circle CenterX=138 CenterY=255 CenterZ=0 NormalX=0 NormalY=0 NormalZ=1 AngleXU=0 Radius=5
    g27: Circle CenterX=156.7 CenterY=255 CenterZ=0 NormalX=0 NormalY=0 NormalZ=1 AngleXU=0 Radius=5
    g28: Circle CenterX=110 CenterY=220 CenterZ=0 NormalX=0 NormalY=0 NormalZ=1 AngleXU=0 Radius=5
    g29: Circle CenterX=184.8 CenterY=220 CenterZ=0 NormalX=0 NormalY=0 NormalZ=1 AngleXU=0 Radius=5
    g30: Circle CenterX=110 CenterY=170 CenterZ=0 NormalX=0 NormalY=0 NormalZ=1 AngleXU=0 Radius=5
    g31: Circle CenterX=184.8 CenterY=170 CenterZ=0 NormalX=0 NormalY=0 NormalZ=1 AngleXU=0 Radius=5
  constraints (86):
    c: Coincident(g0,g1)
    c: Coincident(g1,g2)
    c: Coincident(g2,g3)
    c: Coincident(g3,g0)
    c: Horizontal(g0)
    c: Horizontal(g2)
    c: Vertical(g1)
    c: Vertical(g3)
    c: DistanceX(g2) = 99
    c: DistanceX(g1) = 261
    c: DistanceY(g2) = 40
    c: DistanceY(g0) = 265
    c: Equal(g18,g19)
    c: Equal(g18,g20)
    c: Equal(g18,g23)
    c: Equal(g18,g9)
    c: Equal(g18, g4-g8) x5
    c: Equal(g18, g10-g13) x4
    c: Radius(g18) = 1.25
    c: DistanceX(g7) = 103.5
    c: DistanceY(g7) = 44.4
    c: DistanceX(g7,g6) = 0
    c: DistanceX(g4,g6) = 0
    c: DistanceX(g7,g8) = 153
    c: DistanceY(g7,g8) = 0
    c: DistanceY(g6,g9) = 0
    c: DistanceY(g5,g4) = 0
    c: DistanceX(g8,g9) = 0
    c: DistanceX(g9,g5) = 0
    c: DistanceX(g17) = 196.95
    c: DistanceY(g17) = 149.08
    c: Equal(g14,g16)
    c: Equal(g14,g17)
    c: Equal(g14,g15)
    c: Diameter(g14) = 3.25
    c: DistanceX(g17,g16) = 49
    c: DistanceY(g17,g16) = 0
    c: DistanceY(g17,g15) = 58
    c: DistanceX(g17,g15) = 0
    c: DistanceY(g14,g15) = 0
    c: DistanceX(g14,g16) = 0
    c: DistanceX(g12) = 213.46
    c: DistanceY(g12) = 194.1
    c: DistanceY(g13,g12) = 0
    c: DistanceX(g12,g13) = 18
    c: DistanceX(g10,g12) = 0
    c: DistanceX(g11,g13) = 0
    c: DistanceY(g12,g10) = 35
    c: DistanceY(g11,g10) = 0
    c: Equal(g24,g25)
    c: Equal(g24,g30)
    c: Equal(g24,g31)
    c: Equal(g24, g26-g29) x4
    c: Diameter(g24) = 10
    c: DistanceY(g24) = 105
    c: DistanceY(g25,g24) = 0
    c: DistanceX(g24) = 138
    c: DistanceX(g24,g25) = 18.7
    c: DistanceY(g24,g26) = 150
    c: DistanceX(g26,g24) = 0
    c: DistanceX(g27,g25) = 0
    c: DistanceY(g26,g27) = 0
    c: DistanceX(g30) = 110
    c: DistanceY(g30) = 170
    c: DistanceY(g30,g31) = 0
    c: DistanceX(g30,g31) = 74.8
    c: DistanceY(g30,g28) = 50
    c: DistanceY(g28,g29) = 0
    c: DistanceX(g28,g30) = 0
    c: DistanceX(g31,g29) = 0
    c: DistanceY(g7,g4) = 216
    c: DistanceX(g7,g22) = 97.2
    c: DistanceY(g22,g21) = 0
    c: DistanceX(g22,g21) = 45.5
    c: DistanceY(g22) = 62.1
    c: DistanceX(g7,g19) = 104.7
    c: DistanceY(g19) = 94.58
    c: DistanceX(g18,g19) = 0
    c: DistanceY(g19,g18) = 7
    c: DistanceX(g19,g23) = 30
    c: DistanceY(g23,g19) = 0
    c: DistanceX(g23,g20) = 0
    c: DistanceY(g18,g20) = 0
    c: Equal(g22,g21)
    c: Diameter(g22) = 3.25
    c: DistanceY(g7,g6) = 108
FEATURE [Part::Extrusion] Extrude001
  Base = -> Sketch001
  Dir = (0,-1,-2e-16)
  DirMode = 2
  FaceMakerClass = Part::FaceMakerBullseye
  LengthFwd = 4
  LengthRev = 0
  Placement = pos=(0,0,0) rot=(1,0,0;1.5708rad)
  Solid = true
  Symmetric = false
FEATURE [Part::Box] Box041  label="Cube029"
  AttacherType = Attacher::AttachEngine3D
  Height = 15
  Length = 28
  Placement = pos=(60,-103.5,-81) rot=(0,0,1;0rad)
  Width = 45
FEATURE [Part::Cylinder] Cylinder055
  Angle = 360
  AttacherType = Attacher::AttachEngine3D
  FirstAngle = 0
  Height = 15
  Placement = pos=(73.5,-135,-81) rot=(0,0,1;0rad)
  Radius = 35
  SecondAngle = 0
FEATURE [Part::Sphere] Sphere002  label="rainDome"
  Angle1 = -90
  Angle2 = 90
  Angle3 = 180
  AttacherType = Attacher::AttachEngine3D
  Placement = pos=(73.5,-135,-66) rot=(0.57735,0.57735,0.57735;2.0944rad)
  Radius = 35
FEATURE [Part::MultiFuse] Fusion034  label="rainModule"
  Placement = pos=(53.33,-67.67,0) rot=(0,0,1;0.785398rad)
  Shapes = -> [Sphere002,Cylinder055,Box041]
FEATURE [Part::Sphere] Sphere  label="lightDome"
  Angle1 = -90
  Angle2 = 90
  Angle3 = 180
  AttacherType = Attacher::AttachEngine3D
  Placement = pos=(0,-379,-299) rot=(1,0,0;1.5708rad)
  Radius = 30
FEATURE [Part::Feature] Part__Feature101  label="ANT-868-PW-QW-UFL-BODY001"
  shape: bbox 15.69 x 84 x 15.69 mm, 56 faces (baked)
FEATURE [Part::Feature] Part__Feature102  label="Screw001"
  Placement = pos=(0,-7.05,0) rot=(0,0,1;0rad)
  shape: bbox 7.002 x 7.052 x 7.002 mm, 20 faces (baked)
FEATURE [Part::Feature] Part__Feature103  label="Ring001"
  shape: bbox 9.2 x 6 x 9.2 mm, 8 faces, 2 solids (baked)
FEATURE [Part::Compound] Compound002  label="loraAntenna"
  Links = -> [Part__Feature103,Part__Feature101,Part__Feature102]
  Placement = pos=(-0.5,-512,-305.5) rot=(0.57735,-0.57735,-0.57735;2.0944rad)
FEATURE [Part::Feature] Part__Feature104  label="ips7100"
  Placement = pos=(-24,0,222) rot=(0.999993,-0.003655,0;3.14159rad)
  shape: bbox 48.14 x 14.05 x 44.14 mm, 1935 faces (baked)
FEATURE [Part::Compound] Compound  label="ips7100s"
  Links = -> [Part__Feature104]
  Placement = pos=(23.9969,-267.5,-308) rot=(0,0,1;0.006109rad)
FEATURE [Part::Feature] Part__Feature105  label="Printed Circuit Board"
  shape: bbox 25.4 x 17.78 x 1.6 mm, 42 faces (baked)
FEATURE [Part::Feature] Part__Feature106  label="EAHC2835WD6"
  shape: bbox 3.513 x 2.813 x 0.7485 mm, 108 faces, 4 solids (baked)
FEATURE [Part::Feature] Part__Feature107  label="AS7341 v2"
  Placement = pos=(0,-0.339822,1.6) rot=(0,0,1;0rad)
  shape: bbox 2 x 3.1 x 1.1 mm, 267 faces, 26 solids (baked)
FEATURE [Part::Feature] Part__Feature108  label="CAPC-0805-T0.95-BN v1"
  Placement = pos=(-5.01759,-3.15294,1.6) rot=(0,0,1;0rad)
  shape: bbox 2.1 x 1.35 x 0.95 mm, 42 faces (baked)
FEATURE [Part::Feature] Part__Feature109  label="CAPC-0805-T0.95-BN v002"
  Placement = pos=(-5.48627,2.66154,1.6) rot=(0,0,-1;1.5708rad)
  shape: bbox 1.35 x 2.1 x 0.95 mm, 42 faces (baked)
FEATURE [Part::Feature] Part__Feature110  label="CAPC-0805-T0.95-BN v003"
  Placement = pos=(-3.43627,2.66154,1.6) rot=(0,0,-1;1.5708rad)
  shape: bbox 1.35 x 2.1 x 0.95 mm, 42 faces (baked)
FEATURE [Part::Feature] Part__Feature111  label="CAPC-0603-T0.9-BN v1"
  Placement = pos=(-1.69987,-3.28475,1.6) rot=(0,0,1;0rad)
  shape: bbox 1.7 x 0.9 x 0.9 mm, 42 faces (baked)
FEATURE [Part::Feature] Part__Feature112  label="BODY_MF06A"
  Placement = pos=(0,0,0.762) rot=(0.57735,-0.57735,-0.57735;2.0944rad)
  shape: bbox 1.601 x 2.921 x 1.016 mm, 42 faces (baked)
FEATURE [Part::Feature] Part__Feature113  label="LEAD_MF06A"
  Placement = pos=(-0.9652,-0.9525,0.1016) rot=(0.57735,-0.57735,-0.57735;2.0944rad)
  shape: bbox 0.6223 x 0.3749 x 0.8636 mm, 14 faces (baked)
FEATURE [Part::Feature] Part__Feature114  label="LEAD_MF06A001"
  Placement = pos=(-0.9652,0,0.1016) rot=(0.57735,-0.57735,-0.57735;2.0944rad)
  shape: bbox 0.6223 x 0.3749 x 0.8636 mm, 14 faces (baked)
FEATURE [Part::Feature] Part__Feature115  label="LEAD_MF06A002"
  Placement = pos=(-0.9652,0.9525,0.1016) rot=(0.57735,-0.57735,-0.57735;2.0944rad)
  shape: bbox 0.6223 x 0.3749 x 0.8636 mm, 14 faces (baked)
FEATURE [Part::Feature] Part__Feature116  label="LEAD_MF06A003"
  Placement = pos=(0.9652,-0.9525,0.1016) rot=(0.57735,0.57735,0.57735;2.0944rad)
  shape: bbox 0.6223 x 0.3749 x 0.8636 mm, 14 faces (baked)
FEATURE [Part::Feature] Part__Feature117  label="LEAD_MF06A004"
  Placement = pos=(0.9652,0,0.1016) rot=(0.57735,0.57735,0.57735;2.0944rad)
  shape: bbox 0.6223 x 0.3749 x 0.8636 mm, 14 faces (baked)
FEATURE [Part::Feature] Part__Feature118  label="LEAD_MF06A005"
  Placement = pos=(0.9652,0.9525,0.1016) rot=(0.57735,0.57735,0.57735;2.0944rad)
  shape: bbox 0.6223 x 0.3749 x 0.8636 mm, 14 faces (baked)
FEATURE [Part::Feature] Part__Feature119  label="SOT363 v2"
  Placement = pos=(4.97054,-0.645171,1.675) rot=(0,0,1;3.14159rad)
  shape: bbox 2.1 x 2 x 1.1 mm, 94 faces, 7 solids (baked)
FEATURE [Part::Feature] Part__Feature120  label="LED 0603 single color v1"
  Placement = pos=(-9.18406,3.72778,1.60762) rot=(0,0,1;1.5708rad)
  shape: bbox 1.961 x 0.7932 x 0.7145 mm, 63 faces, 5 solids (baked)
FEATURE [Part::Feature] Part__Feature121  label="RESC-0603 v1"
  Placement = pos=(4.83432,-3.67461,1.6) rot=(0,0,1;0rad)
  shape: bbox 1.7 x 0.9 x 0.55 mm, 52 faces, 3 solids (baked)
FEATURE [Part::Feature] Part__Feature122  label="RESC-0603 v002"
  Placement = pos=(-7.14949,3.61248,1.6) rot=(0,0,-1;1.5708rad)
  shape: bbox 0.9 x 1.7 x 0.55 mm, 52 faces, 3 solids (baked)
FEATURE [Part::Feature] Part__Feature123  label="YC164_RESPACK v1"
  Placement = pos=(2.99591,1.52916,1.6) rot=(0,0,1;0rad)
  shape: bbox 3.2 x 1.6 x 0.61 mm, 172 faces (baked)
FEATURE [Part::Feature] Part__Feature124  label="qwicc v2"
  Placement = pos=(-10.8364,0.0607456,1.65) rot=(0,0,-1;1.5708rad)
  shape: bbox 4.95 x 6 x 2.96 mm, 229 faces, 7 solids (baked)
FEATURE [Part::Feature] Part__Feature125  label="qwicc v003"
  Placement = pos=(10.8256,0.00556102,1.65) rot=(0,0,1;1.5708rad)
  shape: bbox 4.95 x 6 x 2.96 mm, 229 faces, 7 solids (baked)
FEATURE [Part::Feature] Part__Feature126  label="scd30"
  Placement = pos=(1.5,-294,-280) rot=(0,1,0;3.14159rad)
  shape: bbox 35.11 x 7.027 x 23.02 mm, 2292 faces, 25 solids (baked)
FEATURE [App::Part] sot_23_6_v2  label="sot-23-6 v2"
  Group = -> [Part__Feature112,Part__Feature113,Part__Feature114,Part__Feature115,Part__Feature116,Part__Feature117,Part__Feature118]
  Origin = -> Origin008
  Placement = pos=(-4.47945,-0.603742,1.69152) rot=(0,0,1;0rad)
FEATURE [App::Part] Adafruit_AS7341_STEMMA_QT_v2  label="bme280"
  Group = -> [Part__Feature105,Part__Feature106,Part__Feature107,Part__Feature108,Part__Feature109,Part__Feature110,Part__Feature111,sot_23_6_v2,Part__Feature119,Part__Feature120,Part__Feature121,Part__Feature122,Part__Feature123,Part__Feature124,Part__Feature125]
  Origin = -> Origin009
  Placement = pos=(10,-301,-298) rot=(-1,0,0;4.71239rad)
FEATURE [Part::Feature] Part__Feature127  label="Board"
  shape: bbox 25.4 x 25.4 x 1.57 mm, 211 faces (baked)
FEATURE [Part::Feature] Part__Feature128  label="QFN24_4MM"
  Placement = pos=(12.1412,14.4526,1.57) rot=(0,0,1;3.92699rad)
  shape: bbox 5.657 x 5.657 x 0.9 mm, 172 faces (baked)
FEATURE [Part::Feature] Part__Feature129  label="Part 5"
  shape: bbox 0.48 x 0.6603 x 0.6 mm, 14 faces (baked)
FEATURE [Part::Feature] Part__Feature130  label="Part 6"
  shape: bbox 0.48 x 0.6603 x 0.6 mm, 14 faces (baked)
FEATURE [Part::Feature] Part__Feature131  label="Part 4"
  shape: bbox 0.48 x 0.6603 x 0.6 mm, 14 faces (baked)
FEATURE [Part::Feature] Part__Feature132  label="Part 3"
  shape: bbox 0.48 x 0.6603 x 0.6 mm, 14 faces (baked)
FEATURE [Part::Feature] Part__Feature133  label="Part 010"
  shape: bbox 0.48 x 0.6603 x 0.6 mm, 14 faces (baked)
FEATURE [Part::Feature] Part__Feature134  label="Part 011"
  shape: bbox 3 x 1.4 x 1 mm, 10 faces (baked)
FEATURE [Part::Feature] Part__Feature135  label="Pin1"
  shape: bbox 0.6224 x 1.252 x 1.252 mm, 37 faces (baked)
FEATURE [Part::Feature] Part__Feature136  label="Pin2"
  shape: bbox 0.6224 x 1.252 x 1.252 mm, 37 faces (baked)
FEATURE [Part::Feature] Part__Feature137  label="CeramicBody"
  shape: bbox 1.8 x 1.23 x 1.23 mm, 10 faces (baked)
FEATURE [Part::Feature] Part__Feature138  label="0603-NO (1)"
  Placement = pos=(23.241,6.223,1.57) rot=(0,0,1;0rad)
  shape: bbox 1.7 x 0.9 x 0.55 mm, 52 faces, 3 solids (baked)
FEATURE [Part::Feature] Part__Feature139  label="0603-NO (2)"
  Placement = pos=(13.3858,8.4328,1.57) rot=(0,0,1;0rad)
  shape: bbox 1.7 x 0.9 x 0.55 mm, 52 faces, 3 solids (baked)
FEATURE [Part::Feature] Part__Feature140  label="0603-NO (3)"
  Placement = pos=(1.905,18.923,1.57) rot=(0,0,1;3.14159rad)
  shape: bbox 1.7 x 0.9 x 0.55 mm, 52 faces, 3 solids (baked)
FEATURE [Part::Feature] Part__Feature141  label="Pin1 (1)"
  shape: bbox 0.6224 x 1.252 x 1.252 mm, 37 faces (baked)
FEATURE [Part::Feature] Part__Feature142  label="Pin2 (1)"
  shape: bbox 0.6224 x 1.252 x 1.252 mm, 37 faces (baked)
FEATURE [Part::Feature] Part__Feature040  label="CeramicBody (1)"
  shape: bbox 1.8 x 1.23 x 1.23 mm, 10 faces (baked)
FEATURE [Part::Feature] Part__Feature143  label="Pin1 (2)"
  shape: bbox 0.6224 x 1.252 x 1.252 mm, 37 faces (baked)
FEATURE [Part::Feature] Part__Feature144  label="Pin2 (2)"
  shape: bbox 0.6224 x 1.252 x 1.252 mm, 37 faces (baked)
FEATURE [Part::Feature] Part__Feature145  label="CeramicBody (2)"
  shape: bbox 1.8 x 1.23 x 1.23 mm, 10 faces (baked)
FEATURE [Part::Feature] Part__Feature146  label="CHIPLED_0603_NOOUTLINE"
  Placement = pos=(23.368,8.509,1.57) rot=(0,0,1;1.5708rad)
  shape: bbox 1.616 x 0.8 x 0.4 mm, 133 faces (baked)
FEATURE [Part::Feature] Part__Feature147  label="CHIPLED_0603_NOOUTLINE (1)"
  Placement = pos=(1.905,16.764,1.57) rot=(0,0,-1;1.5708rad)
  shape: bbox 1.616 x 0.8 x 0.4 mm, 133 faces (baked)
FEATURE [Part::Feature] Part__Feature148  label="JST_SH4"
  Placement = pos=(22.86,12.7,1.57) rot=(0,0,1;1.5708rad)
  shape: bbox 4.95 x 6 x 2.96 mm, 229 faces, 7 solids (baked)
FEATURE [Part::Feature] Part__Feature149  label="JST_SH4 (1)"
  Placement = pos=(2.54,12.7,1.57) rot=(0,0,-1;1.5708rad)
  shape: bbox 4.95 x 6 x 2.96 mm, 229 faces, 7 solids (baked)
FEATURE [Part::Feature] Part__Feature150  label="NEO3535_REVERSE"
  Placement = pos=(12.7,23.114,0) rot=(0,1,0;3.14159rad)
  shape: bbox 5.88 x 2.8 x 1.78 mm, 41 faces, 5 solids (baked)
FEATURE [Part::Feature] Part__Feature151  label="RESPACK_4X0603"
  Placement = pos=(22.86,18.415,1.57) rot=(0,0,1;3.14159rad)
  shape: bbox 3.2 x 1.6 x 0.61 mm, 172 faces (baked)
FEATURE [Part::Feature] Part__Feature152  label="SOT363"
  Placement = pos=(17.399,12.192,1.57) rot=(0,0,-1;1.5708rad)
  shape: bbox 2.208 x 2.208 x 1.121 mm, 178 faces, 4 solids (baked)
FEATURE [App::Part] _603_NO  label="0603-NO"
  Group = -> [Part__Feature135,Part__Feature136,Part__Feature137]
  Origin = -> Origin012
  Placement = pos=(16.51,8.382,1.57) rot=(0,0,1;0rad)
FEATURE [App::Part] _6700497  label="36700497"
  Group = -> [Part__Feature129,Part__Feature130,Part__Feature131,Part__Feature132,Part__Feature133,Part__Feature134]
  Origin = -> Origin010
  Placement = pos=(0,0,0) rot=(0,0,1;3.14159rad)
FEATURE [App::Part] SOT23_5  label="SOT23-5"
  Group = -> [_6700497]
  Origin = -> Origin011
  Placement = pos=(2.54,6.985,1.57) rot=(0,0,1;3.14159rad)
FEATURE [App::Part] _805_NO  label="0805-NO"
  Group = -> [Part__Feature141,Part__Feature142,Part__Feature040]
  Origin = -> Origin013
  Placement = pos=(7.874,13.589,1.57) rot=(0,0,1;1.5708rad)
FEATURE [App::Part] _805_NO__1_  label="0805-NO (1)"
  Group = -> [Part__Feature143,Part__Feature144,Part__Feature145]
  Origin = -> Origin014
  Placement = pos=(12.827,6.223,1.57) rot=(0,0,1;3.14159rad)
FEATURE [App::Part] Packages
  Group = -> [Part__Feature128,SOT23_5,_603_NO,Part__Feature138,Part__Feature139,Part__Feature140,_805_NO,_805_NO__1_,Part__Feature146,Part__Feature147,Part__Feature148,Part__Feature149,Part__Feature150,Part__Feature151,Part__Feature152]
  Origin = -> Origin015
FEATURE [App::Part] Adafruit_I2C_QT_Rotary_Encoder_v2  label="gps"
  Group = -> [Part__Feature127,Packages]
  Origin = -> Origin016
  Placement = pos=(-7.85,-307,-258) rot=(0,0,1;0rad)
FEATURE [Sketcher::SketchObject] Sketch003  label="inner"
  FullyConstrained = true
  Placement = pos=(0,0,-259.26) rot=(0,0,1;0rad)
  sketch-geometry (4):
    g0: LineSegment StartX=-30 StartY=-277 StartZ=0 EndX=-30 EndY=-327 EndZ=0
    g1: LineSegment StartX=-30 StartY=-327 StartZ=0 EndX=30 EndY=-327 EndZ=0
    g2: LineSegment StartX=30 StartY=-327 StartZ=0 EndX=30 EndY=-277 EndZ=0
    g3: LineSegment StartX=30 StartY=-277 StartZ=0 EndX=-30 EndY=-277 EndZ=0
  constraints (12):
    c: Vertical(g0)
    c: Coincident(g1,g0)
    c: Horizontal(g1)
    c: Coincident(g2,g1)
    c: Vertical(g2)
    c: Coincident(g3,g2)
    c: Coincident(g3,g0)
    c: Horizontal(g3)
    c: DistanceX(g0) = -30
    c: DistanceX(g1) = 30
    c: DistanceY(g0) = -327
    c: DistanceY(g0,g0) = 50
FEATURE [Sketcher::SketchObject] Sketch004  label="outer"
  FullyConstrained = true
  Placement = pos=(0,0,-281.2) rot=(0,0,1;0rad)
  sketch-geometry (4):
    g0: LineSegment StartX=-59 StartY=-252 StartZ=0 EndX=-59 EndY=-352 EndZ=0
    g1: LineSegment StartX=-59 StartY=-352 StartZ=0 EndX=59 EndY=-352 EndZ=0
    g2: LineSegment StartX=59 StartY=-352 StartZ=0 EndX=59 EndY=-252 EndZ=0
    g3: LineSegment StartX=59 StartY=-252 StartZ=0 EndX=-59 EndY=-252 EndZ=0
  constraints (12):
    c: Vertical(g0)
    c: Coincident(g1,g0)
    c: Horizontal(g1)
    c: Coincident(g2,g1)
    c: Vertical(g2)
    c: Coincident(g3,g2)
    c: Coincident(g3,g0)
    c: Horizontal(g3)
    c: DistanceX(g0) = -59
    c: DistanceX(g1) = 59
    c: DistanceY(g0) = -352
    c: DistanceY(g0,g0) = 100
FEATURE [Part::Loft] Loft
  Closed = false
  MaxDegree = 5
  Ruled = false
  Sections = -> [Sketch003,Sketch004]
  Solid = true
FEATURE [Part::Fillet] Fillet
  Base = -> Loft
  Edges = 12 edges r=3: [Edge1,Edge2,Edge3,Edge4,Edge5,Edge6,Edge7,Edge8,Edge9,Edge10,Edge11,Edge12]
FEATURE [Sketcher::SketchObject] Sketch005  label="inner001"
  FullyConstrained = true
  Placement = pos=(0,0,-259.26) rot=(0,0,1;0rad)
  sketch-geometry (4):
    g0: LineSegment StartX=-30 StartY=-277 StartZ=0 EndX=-30 EndY=-327 EndZ=0
    g1: LineSegment StartX=-30 StartY=-327 StartZ=0 EndX=30 EndY=-327 EndZ=0
    g2: LineSegment StartX=30 StartY=-327 StartZ=0 EndX=30 EndY=-277 EndZ=0
    g3: LineSegment StartX=30 StartY=-277 StartZ=0 EndX=-30 EndY=-277 EndZ=0
  constraints (12):
    c: Vertical(g0)
    c: Coincident(g1,g0)
    c: Horizontal(g1)
    c: Coincident(g2,g1)
    c: Vertical(g2)
    c: Coincident(g3,g2)
    c: Coincident(g3,g0)
    c: Horizontal(g3)
    c: DistanceX(g0) = -30
    c: DistanceX(g1) = 30
    c: DistanceY(g0) = -327
    c: DistanceY(g0,g0) = 50
FEATURE [Sketcher::SketchObject] Sketch006  label="outer001"
  FullyConstrained = true
  Placement = pos=(0,0,-281.2) rot=(0,0,1;0rad)
  sketch-geometry (4):
    g0: LineSegment StartX=-59 StartY=-252 StartZ=0 EndX=-59 EndY=-352 EndZ=0
    g1: LineSegment StartX=-59 StartY=-352 StartZ=0 EndX=59 EndY=-352 EndZ=0
    g2: LineSegment StartX=59 StartY=-352 StartZ=0 EndX=59 EndY=-252 EndZ=0
    g3: LineSegment StartX=59 StartY=-252 StartZ=0 EndX=-59 EndY=-252 EndZ=0
  constraints (12):
    c: Vertical(g0)
    c: Coincident(g1,g0)
    c: Horizontal(g1)
    c: Coincident(g2,g1)
    c: Vertical(g2)
    c: Coincident(g3,g2)
    c: Coincident(g3,g0)
    c: Horizontal(g3)
    c: DistanceX(g0) = -59
    c: DistanceX(g1) = 59
    c: DistanceY(g0) = -352
    c: DistanceY(g0,g0) = 100
FEATURE [Part::Loft] Loft001
  Closed = false
  MaxDegree = 5
  Ruled = false
  Sections = -> [Sketch005,Sketch006]
  Solid = true
FEATURE [Part::Fillet] Fillet009
  Base = -> Loft001
  Edges = 12 edges r=3: [Edge1,Edge2,Edge3,Edge4,Edge5,Edge6,Edge7,Edge8,Edge9,Edge10,Edge11,Edge12]
  Placement = pos=(0,0,-4) rot=(0,0,1;0rad)
FEATURE [Part::Cut] Cut  label="sls01"
  Base = -> Fillet
  Tool = -> Fillet009
FEATURE [Sketcher::SketchObject] Sketch007  label="inner002"
  FullyConstrained = true
  Placement = pos=(0,0,-259.26) rot=(0,0,1;0rad)
  sketch-geometry (4):
    g0: LineSegment StartX=-30 StartY=-277 StartZ=0 EndX=-30 EndY=-327 EndZ=0
    g1: LineSegment StartX=-30 StartY=-327 StartZ=0 EndX=30 EndY=-327 EndZ=0
    g2: LineSegment StartX=30 StartY=-327 StartZ=0 EndX=30 EndY=-277 EndZ=0
    g3: LineSegment StartX=30 StartY=-277 StartZ=0 EndX=-30 EndY=-277 EndZ=0
  constraints (12):
    c: Vertical(g0)
    c: Coincident(g1,g0)
    c: Horizontal(g1)
    c: Coincident(g2,g1)
    c: Vertical(g2)
    c: Coincident(g3,g2)
    c: Coincident(g3,g0)
    c: Horizontal(g3)
    c: DistanceX(g0) = -30
    c: DistanceX(g1) = 30
    c: DistanceY(g0) = -327
    c: DistanceY(g0,g0) = 50
FEATURE [Sketcher::SketchObject] Sketch008  label="outer002"
  FullyConstrained = true
  Placement = pos=(0,0,-281.2) rot=(0,0,1;0rad)
  sketch-geometry (4):
    g0: LineSegment StartX=-59 StartY=-252 StartZ=0 EndX=-59 EndY=-352 EndZ=0
    g1: LineSegment StartX=-59 StartY=-352 StartZ=0 EndX=59 EndY=-352 EndZ=0
    g2: LineSegment StartX=59 StartY=-352 StartZ=0 EndX=59 EndY=-252 EndZ=0
    g3: LineSegment StartX=59 StartY=-252 StartZ=0 EndX=-59 EndY=-252 EndZ=0
  constraints (12):
    c: Vertical(g0)
    c: Coincident(g1,g0)
    c: Horizontal(g1)
    c: Coincident(g2,g1)
    c: Vertical(g2)
    c: Coincident(g3,g2)
    c: Coincident(g3,g0)
    c: Horizontal(g3)
    c: DistanceX(g0) = -59
    c: DistanceX(g1) = 59
    c: DistanceY(g0) = -352
    c: DistanceY(g0,g0) = 100
FEATURE [Part::Loft] Loft002
  Closed = false
  MaxDegree = 5
  Ruled = false
  Sections = -> [Sketch007,Sketch008]
  Solid = true
FEATURE [Part::Fillet] Fillet010
  Base = -> Loft002
  Edges = 12 edges r=3: [Edge1,Edge2,Edge3,Edge4,Edge5,Edge6,Edge7,Edge8,Edge9,Edge10,Edge11,Edge12]
FEATURE [Sketcher::SketchObject] Sketch009  label="inner003"
  FullyConstrained = true
  Placement = pos=(0,0,-259.26) rot=(0,0,1;0rad)
  sketch-geometry (4):
    g0: LineSegment StartX=-30 StartY=-277 StartZ=0 EndX=-30 EndY=-327 EndZ=0
    g1: LineSegment StartX=-30 StartY=-327 StartZ=0 EndX=30 EndY=-327 EndZ=0
    g2: LineSegment StartX=30 StartY=-327 StartZ=0 EndX=30 EndY=-277 EndZ=0
    g3: LineSegment StartX=30 StartY=-277 StartZ=0 EndX=-30 EndY=-277 EndZ=0
  constraints (12):
    c: Vertical(g0)
    c: Coincident(g1,g0)
    c: Horizontal(g1)
    c: Coincident(g2,g1)
    c: Vertical(g2)
    c: Coincident(g3,g2)
    c: Coincident(g3,g0)
    c: Horizontal(g3)
    c: DistanceX(g0) = -30
    c: DistanceX(g1) = 30
    c: DistanceY(g0) = -327
    c: DistanceY(g0,g0) = 50
FEATURE [Sketcher::SketchObject] Sketch010  label="outer003"
  FullyConstrained = true
  Placement = pos=(0,0,-281.2) rot=(0,0,1;0rad)
  sketch-geometry (4):
    g0: LineSegment StartX=-59 StartY=-252 StartZ=0 EndX=-59 EndY=-352 EndZ=0
    g1: LineSegment StartX=-59 StartY=-352 StartZ=0 EndX=59 EndY=-352 EndZ=0
    g2: LineSegment StartX=59 StartY=-352 StartZ=0 EndX=59 EndY=-252 EndZ=0
    g3: LineSegment StartX=59 StartY=-252 StartZ=0 EndX=-59 EndY=-252 EndZ=0
  constraints (12):
    c: Vertical(g0)
    c: Coincident(g1,g0)
    c: Horizontal(g1)
    c: Coincident(g2,g1)
    c: Vertical(g2)
    c: Coincident(g3,g2)
    c: Coincident(g3,g0)
    c: Horizontal(g3)
    c: DistanceX(g0) = -59
    c: DistanceX(g1) = 59
    c: DistanceY(g0) = -352
    c: DistanceY(g0,g0) = 100
FEATURE [Part::Loft] Loft003
  Closed = false
  MaxDegree = 5
  Ruled = false
  Sections = -> [Sketch009,Sketch010]
  Solid = true
FEATURE [Part::Fillet] Fillet011
  Base = -> Loft003
  Edges = 12 edges r=3: [Edge1,Edge2,Edge3,Edge4,Edge5,Edge6,Edge7,Edge8,Edge9,Edge10,Edge11,Edge12]
  Placement = pos=(0,0,-4) rot=(0,0,1;0rad)
FEATURE [Part::Cut] Cut004  label="sls002"
  Base = -> Fillet010
  Placement = pos=(0,0,-16) rot=(0,0,1;0rad)
  Tool = -> Fillet011
FEATURE [Sketcher::SketchObject] Sketch011  label="inner004"
  FullyConstrained = true
  Placement = pos=(0,0,-259.26) rot=(0,0,1;0rad)
  sketch-geometry (4):
    g0: LineSegment StartX=-30 StartY=-277 StartZ=0 EndX=-30 EndY=-327 EndZ=0
    g1: LineSegment StartX=-30 StartY=-327 StartZ=0 EndX=30 EndY=-327 EndZ=0
    g2: LineSegment StartX=30 StartY=-327 StartZ=0 EndX=30 EndY=-277 EndZ=0
    g3: LineSegment StartX=30 StartY=-277 StartZ=0 EndX=-30 EndY=-277 EndZ=0
  constraints (12):
    c: Vertical(g0)
    c: Coincident(g1,g0)
    c: Horizontal(g1)
    c: Coincident(g2,g1)
    c: Vertical(g2)
    c: Coincident(g3,g2)
    c: Coincident(g3,g0)
    c: Horizontal(g3)
    c: DistanceX(g0) = -30
    c: DistanceX(g1) = 30
    c: DistanceY(g0) = -327
    c: DistanceY(g0,g0) = 50
FEATURE [Sketcher::SketchObject] Sketch012  label="outer004"
  FullyConstrained = true
  Placement = pos=(0,0,-281.2) rot=(0,0,1;0rad)
  sketch-geometry (4):
    g0: LineSegment StartX=-59 StartY=-252 StartZ=0 EndX=-59 EndY=-352 EndZ=0
    g1: LineSegment StartX=-59 StartY=-352 StartZ=0 EndX=59 EndY=-352 EndZ=0
    g2: LineSegment StartX=59 StartY=-352 StartZ=0 EndX=59 EndY=-252 EndZ=0
    g3: LineSegment StartX=59 StartY=-252 StartZ=0 EndX=-59 EndY=-252 EndZ=0
  constraints (12):
    c: Vertical(g0)
    c: Coincident(g1,g0)
    c: Horizontal(g1)
    c: Coincident(g2,g1)
    c: Vertical(g2)
    c: Coincident(g3,g2)
    c: Coincident(g3,g0)
    c: Horizontal(g3)
    c: DistanceX(g0) = -59
    c: DistanceX(g1) = 59
    c: DistanceY(g0) = -352
    c: DistanceY(g0,g0) = 100
FEATURE [Part::Loft] Loft004
  Closed = false
  MaxDegree = 5
  Ruled = false
  Sections = -> [Sketch011,Sketch012]
  Solid = true
FEATURE [Part::Fillet] Fillet012
  Base = -> Loft004
  Edges = 12 edges r=3: [Edge1,Edge2,Edge3,Edge4,Edge5,Edge6,Edge7,Edge8,Edge9,Edge10,Edge11,Edge12]
FEATURE [Sketcher::SketchObject] Sketch013  label="inner005"
  FullyConstrained = true
  Placement = pos=(0,0,-259.26) rot=(0,0,1;0rad)
  sketch-geometry (4):
    g0: LineSegment StartX=-30 StartY=-277 StartZ=0 EndX=-30 EndY=-327 EndZ=0
    g1: LineSegment StartX=-30 StartY=-327 StartZ=0 EndX=30 EndY=-327 EndZ=0
    g2: LineSegment StartX=30 StartY=-327 StartZ=0 EndX=30 EndY=-277 EndZ=0
    g3: LineSegment StartX=30 StartY=-277 StartZ=0 EndX=-30 EndY=-277 EndZ=0
  constraints (12):
    c: Vertical(g0)
    c: Coincident(g1,g0)
    c: Horizontal(g1)
    c: Coincident(g2,g1)
    c: Vertical(g2)
    c: Coincident(g3,g2)
    c: Coincident(g3,g0)
    c: Horizontal(g3)
    c: DistanceX(g0) = -30
    c: DistanceX(g1) = 30
    c: DistanceY(g0) = -327
    c: DistanceY(g0,g0) = 50
FEATURE [Sketcher::SketchObject] Sketch014  label="outer005"
  FullyConstrained = true
  Placement = pos=(0,0,-281.2) rot=(0,0,1;0rad)
  sketch-geometry (4):
    g0: LineSegment StartX=-59 StartY=-252 StartZ=0 EndX=-59 EndY=-352 EndZ=0
    g1: LineSegment StartX=-59 StartY=-352 StartZ=0 EndX=59 EndY=-352 EndZ=0
    g2: LineSegment StartX=59 StartY=-352 StartZ=0 EndX=59 EndY=-252 EndZ=0
    g3: LineSegment StartX=59 StartY=-252 StartZ=0 EndX=-59 EndY=-252 EndZ=0
  constraints (12):
    c: Vertical(g0)
    c: Coincident(g1,g0)
    c: Horizontal(g1)
    c: Coincident(g2,g1)
    c: Vertical(g2)
    c: Coincident(g3,g2)
    c: Coincident(g3,g0)
    c: Horizontal(g3)
    c: DistanceX(g0) = -59
    c: DistanceX(g1) = 59
    c: DistanceY(g0) = -352
    c: DistanceY(g0,g0) = 100
FEATURE [Part::Loft] Loft005
  Closed = false
  MaxDegree = 5
  Ruled = false
  Sections = -> [Sketch013,Sketch014]
  Solid = true
FEATURE [Part::Fillet] Fillet013
  Base = -> Loft005
  Edges = 12 edges r=3: [Edge1,Edge2,Edge3,Edge4,Edge5,Edge6,Edge7,Edge8,Edge9,Edge10,Edge11,Edge12]
  Placement = pos=(0,0,-4) rot=(0,0,1;0rad)
FEATURE [Part::Cut] Cut005  label="sls003"
  Base = -> Fillet012
  Placement = pos=(0,0,-32) rot=(0,0,1;0rad)
  Tool = -> Fillet013
FEATURE [Sketcher::SketchObject] Sketch015  label="inner006"
  FullyConstrained = true
  Placement = pos=(0,0,-259.26) rot=(0,0,1;0rad)
  sketch-geometry (4):
    g0: LineSegment StartX=-30 StartY=-277 StartZ=0 EndX=-30 EndY=-327 EndZ=0
    g1: LineSegment StartX=-30 StartY=-327 StartZ=0 EndX=30 EndY=-327 EndZ=0
    g2: LineSegment StartX=30 StartY=-327 StartZ=0 EndX=30 EndY=-277 EndZ=0
    g3: LineSegment StartX=30 StartY=-277 StartZ=0 EndX=-30 EndY=-277 EndZ=0
  constraints (12):
    c: Vertical(g0)
    c: Coincident(g1,g0)
    c: Horizontal(g1)
    c: Coincident(g2,g1)
    c: Vertical(g2)
    c: Coincident(g3,g2)
    c: Coincident(g3,g0)
    c: Horizontal(g3)
    c: DistanceX(g0) = -30
    c: DistanceX(g1) = 30
    c: DistanceY(g0) = -327
    c: DistanceY(g0,g0) = 50
FEATURE [Sketcher::SketchObject] Sketch016  label="outer006"
  FullyConstrained = true
  Placement = pos=(0,0,-281.2) rot=(0,0,1;0rad)
  sketch-geometry (4):
    g0: LineSegment StartX=-59 StartY=-252 StartZ=0 EndX=-59 EndY=-352 EndZ=0
    g1: LineSegment StartX=-59 StartY=-352 StartZ=0 EndX=59 EndY=-352 EndZ=0
    g2: LineSegment StartX=59 StartY=-352 StartZ=0 EndX=59 EndY=-252 EndZ=0
    g3: LineSegment StartX=59 StartY=-252 StartZ=0 EndX=-59 EndY=-252 EndZ=0
  constraints (12):
    c: Vertical(g0)
    c: Coincident(g1,g0)
    c: Horizontal(g1)
    c: Coincident(g2,g1)
    c: Vertical(g2)
    c: Coincident(g3,g2)
    c: Coincident(g3,g0)
    c: Horizontal(g3)
    c: DistanceX(g0) = -59
    c: DistanceX(g1) = 59
    c: DistanceY(g0) = -352
    c: DistanceY(g0,g0) = 100
FEATURE [Part::Loft] Loft006
  Closed = false
  MaxDegree = 5
  Ruled = false
  Sections = -> [Sketch015,Sketch016]
  Solid = true
FEATURE [Part::Fillet] Fillet014
  Base = -> Loft006
  Edges = 12 edges r=3: [Edge1,Edge2,Edge3,Edge4,Edge5,Edge6,Edge7,Edge8,Edge9,Edge10,Edge11,Edge12]
FEATURE [Sketcher::SketchObject] Sketch017  label="inner007"
  FullyConstrained = true
  Placement = pos=(0,0,-259.26) rot=(0,0,1;0rad)
  sketch-geometry (4):
    g0: LineSegment StartX=-30 StartY=-277 StartZ=0 EndX=-30 EndY=-327 EndZ=0
    g1: LineSegment StartX=-30 StartY=-327 StartZ=0 EndX=30 EndY=-327 EndZ=0
    g2: LineSegment StartX=30 StartY=-327 StartZ=0 EndX=30 EndY=-277 EndZ=0
    g3: LineSegment StartX=30 StartY=-277 StartZ=0 EndX=-30 EndY=-277 EndZ=0
  constraints (12):
    c: Vertical(g0)
    c: Coincident(g1,g0)
    c: Horizontal(g1)
    c: Coincident(g2,g1)
    c: Vertical(g2)
    c: Coincident(g3,g2)
    c: Coincident(g3,g0)
    c: Horizontal(g3)
    c: DistanceX(g0) = -30
    c: DistanceX(g1) = 30
    c: DistanceY(g0) = -327
    c: DistanceY(g0,g0) = 50
FEATURE [Sketcher::SketchObject] Sketch018  label="outer007"
  FullyConstrained = true
  Placement = pos=(0,0,-281.2) rot=(0,0,1;0rad)
  sketch-geometry (4):
    g0: LineSegment StartX=-59 StartY=-252 StartZ=0 EndX=-59 EndY=-352 EndZ=0
    g1: LineSegment StartX=-59 StartY=-352 StartZ=0 EndX=59 EndY=-352 EndZ=0
    g2: LineSegment StartX=59 StartY=-352 StartZ=0 EndX=59 EndY=-252 EndZ=0
    g3: LineSegment StartX=59 StartY=-252 StartZ=0 EndX=-59 EndY=-252 EndZ=0
  constraints (12):
    c: Vertical(g0)
    c: Coincident(g1,g0)
    c: Horizontal(g1)
    c: Coincident(g2,g1)
    c: Vertical(g2)
    c: Coincident(g3,g2)
    c: Coincident(g3,g0)
    c: Horizontal(g3)
    c: DistanceX(g0) = -59
    c: DistanceX(g1) = 59
    c: DistanceY(g0) = -352
    c: DistanceY(g0,g0) = 100
FEATURE [Part::Loft] Loft007
  Closed = false
  MaxDegree = 5
  Ruled = false
  Sections = -> [Sketch017,Sketch018]
  Solid = true
FEATURE [Part::Fillet] Fillet015
  Base = -> Loft007
  Edges = 12 edges r=3: [Edge1,Edge2,Edge3,Edge4,Edge5,Edge6,Edge7,Edge8,Edge9,Edge10,Edge11,Edge12]
  Placement = pos=(0,0,-4) rot=(0,0,1;0rad)
FEATURE [Part::Cut] Cut006  label="sls004"
  Base = -> Fillet014
  Placement = pos=(0,0,-48) rot=(0,0,1;0rad)
  Tool = -> Fillet015
FEATURE [Part::Feature] Part__Feature153  label="logoTopCut"
  Placement = pos=(-30.8,-333,-323.9) rot=(0,0,1;0rad)
  shape: bbox 22.79 x 8 x 17.08 mm, 886 faces (baked)
FEATURE [Mesh::Feature] mintsLogo80P___90CutBase  label="mintsLogo80P - 90CutBase"
  Placement = pos=(0.5,-306.5,-309) rot=(1,0,0;1.5708rad)
FEATURE [Sketcher::SketchObject] Sketch019
  FullyConstrained = true
  Placement = pos=(0,-295,0) rot=(1,0,0;1.5708rad)
  sketch-geometry (14):
    g0: LineSegment StartX=28 StartY=-309 StartZ=0 EndX=28 EndY=-301 EndZ=0
    g1: LineSegment StartX=-19 StartY=-309 StartZ=0 EndX=28 EndY=-309 EndZ=0
    g2: LineSegment StartX=-19 StartY=-309 StartZ=0 EndX=-19 EndY=-284 EndZ=0
    g3: LineSegment StartX=-19 StartY=-284 StartZ=0 EndX=-13 EndY=-284 EndZ=0
    g4: LineSegment StartX=-13 StartY=-284 StartZ=0 EndX=-13 EndY=-301 EndZ=0
    g5: Circle CenterX=-15.96 CenterY=-286.8 CenterZ=0 NormalX=0 NormalY=0 NormalZ=1 AngleXU=0 Radius=1.125
    g6: Circle CenterX=-0.15 CenterY=-304.37 CenterZ=0 NormalX=0 NormalY=0 NormalZ=1 AngleXU=0 Radius=1.125
    g7: Circle CenterX=20.15 CenterY=-304.37 CenterZ=0 NormalX=0 NormalY=0 NormalZ=1 AngleXU=0 Radius=1.125
    g8: LineSegment StartX=-13 StartY=-301 StartZ=0 EndX=11 EndY=-301 EndZ=0
    g9: LineSegment StartX=11 StartY=-301 StartZ=0 EndX=11 EndY=-263 EndZ=0
    g10: LineSegment StartX=11 StartY=-263 StartZ=0 EndX=19 EndY=-263 EndZ=0
    g11: LineSegment StartX=19 StartY=-263 StartZ=0 EndX=19 EndY=-301 EndZ=0
    g12: LineSegment StartX=19 StartY=-301 StartZ=0 EndX=28 EndY=-301 EndZ=0
    g13: Circle CenterX=16.04 CenterY=-270.55 CenterZ=0 NormalX=0 NormalY=0 NormalZ=1 AngleXU=0 Radius=1.125
  constraints (42):
    c: Vertical(g0)
    c: Coincident(g1,g0)
    c: Horizontal(g1)
    c: DistanceX(g0) = 28
    c: Vertical(g2)
    c: Coincident(g3,g2)
    c: Horizontal(g3)
    c: Coincident(g4,g3)
    c: Vertical(g4)
    c: DistanceY(g1,g6) = 4.63
    c: DistanceY(g6,g7) = 0
    c: DistanceX(g6,g7) = 20.3
    c: DistanceY(g1) = -309
    c: Coincident(g2,g1)
    c: Coincident(g8,g4)
    c: Horizontal(g8)
    c: DistanceX(g4) = -13
    c: Vertical(g9)
    c: Distance(g3) = 6
    c: Coincident(g10,g9)
    c: Horizontal(g10)
    c: Coincident(g11,g10)
    c: Vertical(g11)
    c: Coincident(g12,g0)
    c: Horizontal(g12)
    c: DistanceY(g8,g11) = 0
    c: Coincident(g11,g12)
    c: DistanceX(g10) = 19
    c: DistanceX(g10,g10) = 8
    c: Coincident(g8,g9)
    c: DistanceY(g9) = -263
    c: DistanceY(g1,g4) = 8
    c: DistanceY(g1,g2) = 25
    c: DistanceX(g5,g13) = 32
    c: DistanceY(g5,g13) = 16.25
    c: DistanceY(g1,g5) = 22.2
    c: DistanceX(g1,g5) = 3.04
    c: Equal(g6,g7)
    c: Equal(g6,g5)
    c: Equal(g6,g13)
    c: Diameter(g6) = 2.25
    c: DistanceX(g6) = -0.15
FEATURE [Part::Extrusion] Extrude003  label="i2cHold"
  Base = -> Sketch019
  Dir = (0,-1,2e-16)
  DirMode = 2
  FaceMakerClass = Part::FaceMakerBullseye
  LengthFwd = 5
  LengthRev = 0
  Solid = true
  Symmetric = false
FEATURE [Sketcher::SketchObject] Sketch020
  FullyConstrained = true
  Placement = pos=(0,0,-263) rot=(0,0,1;0rad)
  sketch-geometry (6):
    g0: LineSegment StartX=11 StartY=-281.5 StartZ=0 EndX=19 EndY=-281.5 EndZ=0
    g1: LineSegment StartX=11 StartY=-281.5 StartZ=0 EndX=11 EndY=-307 EndZ=0
    g2: LineSegment StartX=11 StartY=-307 StartZ=0 EndX=19 EndY=-307 EndZ=0
    g3: LineSegment StartX=19 StartY=-307 StartZ=0 EndX=19 EndY=-281.5 EndZ=0
    g4: Circle CenterX=15 CenterY=-284.1 CenterZ=0 NormalX=0 NormalY=0 NormalZ=1 AngleXU=0 Radius=1.625
    g5: Circle CenterX=15 CenterY=-304.5 CenterZ=0 NormalX=0 NormalY=0 NormalZ=1 AngleXU=0 Radius=1.625
  constraints (18):
    c: Horizontal(g0)
    c: Coincident(g1,g0)
    c: Vertical(g1)
    c: Coincident(g2,g1)
    c: Horizontal(g2)
    c: Coincident(g3,g2)
    c: Coincident(g3,g0)
    c: Vertical(g3)
    c: DistanceX(g1,g2) = 8
    c: DistanceY(g1,g0) = 25.5
    c: Equal(g5,g4)
    c: Diameter(g5) = 3.25
    c: DistanceY(g5,g4) = 20.4
    c: DistanceX(g5,g4) = 0
    c: DistanceY(g1) = -307
    c: DistanceX(g1) = 11
    c: DistanceX(g1,g5) = 4
    c: DistanceY(g1,g5) = 2.5
FEATURE [Part::Extrusion] Extrude004  label="gpsHold"
  Base = -> Sketch020
  Dir = (0,0,1)
  DirMode = 2
  FaceMakerClass = Part::FaceMakerBullseye
  LengthFwd = 5
  LengthRev = 0
  Solid = true
  Symmetric = false
FEATURE [Sketcher::SketchObject] Sketch021
  FullyConstrained = true
  MapMode = 3
  Placement = pos=(0,0,0) rot=(1,0,0;1.5708rad)
  Support = -> [Extrude003]
  sketch-geometry (8):
    g0: LineSegment StartX=-25 StartY=-309 StartZ=0 EndX=-25 EndY=-301 EndZ=0
    g1: LineSegment StartX=-25 StartY=-301 StartZ=0 EndX=16.5 EndY=-301 EndZ=0
    g2: LineSegment StartX=16.5 StartY=-301 StartZ=0 EndX=16.5 EndY=-263 EndZ=0
    g3: LineSegment StartX=16.5 StartY=-263 StartZ=0 EndX=24.5 EndY=-263 EndZ=0
    g4: LineSegment StartX=24.5 StartY=-263 StartZ=0 EndX=24.5 EndY=-309 EndZ=0
    g5: LineSegment StartX=-25 StartY=-309 StartZ=0 EndX=24.5 EndY=-309 EndZ=0
    g6: Circle CenterX=-20.4 CenterY=-304.4 CenterZ=0 NormalX=0 NormalY=0 NormalZ=1 AngleXU=0 Radius=1.125
    g7: Circle CenterX=20.4 CenterY=-267.6 CenterZ=0 NormalX=0 NormalY=0 NormalZ=1 AngleXU=0 Radius=1.125
  constraints (24):
    c: Vertical(g0)
    c: Coincident(g1,g0)
    c: Horizontal(g1)
    c: Coincident(g2,g1)
    c: Vertical(g2)
    c: Coincident(g3,g2)
    c: Horizontal(g3)
    c: Coincident(g4,g3)
    c: Vertical(g4)
    c: Coincident(g5,g0)
    c: Coincident(g5,g4)
    c: Horizontal(g5)
    c: DistanceX(g0) = -25
    c: DistanceY(g0,g0) = 8
    c: DistanceX(g0,g1) = 41.5
    c: DistanceX(g1,g3) = 8
    c: DistanceY(g1,g2) = 38
    c: Equal(g7,g6)
    c: Diameter(g7) = 2.25
    c: DistanceX(g0,g6) = 4.6
    c: DistanceX(g6,g7) = 40.8
    c: DistanceY(g6,g7) = 36.8
    c: DistanceY(g0,g6) = 4.6
    c: DistanceY(g0) = -309
FEATURE [Sketcher::SketchObject] Sketch023
  FullyConstrained = true
  sketch-geometry (4):
    g0: Circle CenterX=-35 CenterY=-332 CenterZ=0 NormalX=0 NormalY=0 NormalZ=1 AngleXU=0 Radius=5.5
    g1: Circle CenterX=35 CenterY=-332 CenterZ=0 NormalX=0 NormalY=0 NormalZ=1 AngleXU=0 Radius=5.5
    g2: Circle CenterX=35 CenterY=-272 CenterZ=0 NormalX=0 NormalY=0 NormalZ=1 AngleXU=0 Radius=5.5
    g3: Circle CenterX=-35 CenterY=-272 CenterZ=0 NormalX=0 NormalY=0 NormalZ=1 AngleXU=0 Radius=5.5
  constraints (12):
    c: DistanceX(g0) = -35
    c: DistanceY(g0) = -332
    c: Equal(g0,g3)
    c: Equal(g0,g2)
    c: Equal(g0,g1)
    c: Diameter(g0) = 11
    c: DistanceX(g3,g0) = 0
    c: DistanceY(g0,g3) = 60
    c: DistanceY(g2,g3) = 0
    c: DistanceY(g0,g1) = 0
    c: DistanceX(g2,g1) = 0
    c: DistanceX(g1) = 35
FEATURE [Part::Extrusion] Extrude007  label="stands"
  Base = -> Sketch023
  Dir = (0,0,1)
  DirMode = 2
  FaceMakerClass = Part::FaceMakerBullseye
  LengthFwd = 69
  LengthRev = 0
  Placement = pos=(0,0,-323) rot=(0,0,1;0rad)
  Solid = true
  Symmetric = false
FEATURE [Sketcher::SketchObject] Sketch024  label="inner008"
  FullyConstrained = true
  Placement = pos=(0,0,-259.26) rot=(0,0,1;0rad)
  sketch-geometry (4):
    g0: LineSegment StartX=-30 StartY=-277 StartZ=0 EndX=-30 EndY=-327 EndZ=0
    g1: LineSegment StartX=-30 StartY=-327 StartZ=0 EndX=30 EndY=-327 EndZ=0
    g2: LineSegment StartX=30 StartY=-327 StartZ=0 EndX=30 EndY=-277 EndZ=0
    g3: LineSegment StartX=30 StartY=-277 StartZ=0 EndX=-30 EndY=-277 EndZ=0
  constraints (12):
    c: Vertical(g0)
    c: Coincident(g1,g0)
    c: Horizontal(g1)
    c: Coincident(g2,g1)
    c: Vertical(g2)
    c: Coincident(g3,g2)
    c: Coincident(g3,g0)
    c: Horizontal(g3)
    c: DistanceX(g0) = -30
    c: DistanceX(g1) = 30
    c: DistanceY(g0) = -327
    c: DistanceY(g0,g0) = 50
FEATURE [Sketcher::SketchObject] Sketch025  label="outer008"
  FullyConstrained = true
  Placement = pos=(0,0,-281.2) rot=(0,0,1;0rad)
  sketch-geometry (4):
    g0: LineSegment StartX=-59 StartY=-252 StartZ=0 EndX=-59 EndY=-352 EndZ=0
    g1: LineSegment StartX=-59 StartY=-352 StartZ=0 EndX=59 EndY=-352 EndZ=0
    g2: LineSegment StartX=59 StartY=-352 StartZ=0 EndX=59 EndY=-252 EndZ=0
    g3: LineSegment StartX=59 StartY=-252 StartZ=0 EndX=-59 EndY=-252 EndZ=0
  constraints (12):
    c: Vertical(g0)
    c: Coincident(g1,g0)
    c: Horizontal(g1)
    c: Coincident(g2,g1)
    c: Vertical(g2)
    c: Coincident(g3,g2)
    c: Coincident(g3,g0)
    c: Horizontal(g3)
    c: DistanceX(g0) = -59
    c: DistanceX(g1) = 59
    c: DistanceY(g0) = -352
    c: DistanceY(g0,g0) = 100
FEATURE [Part::Loft] Loft008
  Closed = false
  MaxDegree = 5
  Ruled = false
  Sections = -> [Sketch024,Sketch025]
  Solid = true
FEATURE [Part::Fillet] Fillet016
  Base = -> Loft008
  Edges = 12 edges r=3: [Edge1,Edge2,Edge3,Edge4,Edge5,Edge6,Edge7,Edge8,Edge9,Edge10,Edge11,Edge12]
FEATURE [Sketcher::SketchObject] Sketch026  label="inner009"
  FullyConstrained = true
  Placement = pos=(0,0,-259.26) rot=(0,0,1;0rad)
  sketch-geometry (4):
    g0: LineSegment StartX=-30 StartY=-277 StartZ=0 EndX=-30 EndY=-327 EndZ=0
    g1: LineSegment StartX=-30 StartY=-327 StartZ=0 EndX=30 EndY=-327 EndZ=0
    g2: LineSegment StartX=30 StartY=-327 StartZ=0 EndX=30 EndY=-277 EndZ=0
    g3: LineSegment StartX=30 StartY=-277 StartZ=0 EndX=-30 EndY=-277 EndZ=0
  constraints (12):
    c: Vertical(g0)
    c: Coincident(g1,g0)
    c: Horizontal(g1)
    c: Coincident(g2,g1)
    c: Vertical(g2)
    c: Coincident(g3,g2)
    c: Coincident(g3,g0)
    c: Horizontal(g3)
    c: DistanceX(g0) = -30
    c: DistanceX(g1) = 30
    c: DistanceY(g0) = -327
    c: DistanceY(g0,g0) = 50
FEATURE [Sketcher::SketchObject] Sketch027  label="outer009"
  FullyConstrained = true
  Placement = pos=(0,0,-281.2) rot=(0,0,1;0rad)
  sketch-geometry (4):
    g0: LineSegment StartX=-59 StartY=-252 StartZ=0 EndX=-59 EndY=-352 EndZ=0
    g1: LineSegment StartX=-59 StartY=-352 StartZ=0 EndX=59 EndY=-352 EndZ=0
    g2: LineSegment StartX=59 StartY=-352 StartZ=0 EndX=59 EndY=-252 EndZ=0
    g3: LineSegment StartX=59 StartY=-252 StartZ=0 EndX=-59 EndY=-252 EndZ=0
  constraints (12):
    c: Vertical(g0)
    c: Coincident(g1,g0)
    c: Horizontal(g1)
    c: Coincident(g2,g1)
    c: Vertical(g2)
    c: Coincident(g3,g2)
    c: Coincident(g3,g0)
    c: Horizontal(g3)
    c: DistanceX(g0) = -59
    c: DistanceX(g1) = 59
    c: DistanceY(g0) = -352
    c: DistanceY(g0,g0) = 100
FEATURE [Part::Loft] Loft009
  Closed = false
  MaxDegree = 5
  Ruled = false
  Sections = -> [Sketch026,Sketch027]
  Solid = true
FEATURE [Part::Fillet] Fillet017
  Base = -> Loft009
  Edges = 12 edges r=3: [Edge1,Edge2,Edge3,Edge4,Edge5,Edge6,Edge7,Edge8,Edge9,Edge10,Edge11,Edge12]
  Placement = pos=(0,0,-4) rot=(0,0,1;0rad)
FEATURE [Part::Cut] Cut007  label="sls005"
  Base = -> Fillet016
  Placement = pos=(0,0,4) rot=(0,0,1;0rad)
  Tool = -> Fillet017
FEATURE [Sketcher::SketchObject] Sketch028  label="inner010"
  FullyConstrained = true
  Placement = pos=(0,0,-259.26) rot=(0,0,1;0rad)
  sketch-geometry (4):
    g0: LineSegment StartX=-30 StartY=-277 StartZ=0 EndX=-30 EndY=-327 EndZ=0
    g1: LineSegment StartX=-30 StartY=-327 StartZ=0 EndX=30 EndY=-327 EndZ=0
    g2: LineSegment StartX=30 StartY=-327 StartZ=0 EndX=30 EndY=-277 EndZ=0
    g3: LineSegment StartX=30 StartY=-277 StartZ=0 EndX=-30 EndY=-277 EndZ=0
  constraints (12):
    c: Vertical(g0)
    c: Coincident(g1,g0)
    c: Horizontal(g1)
    c: Coincident(g2,g1)
    c: Vertical(g2)
    c: Coincident(g3,g2)
    c: Coincident(g3,g0)
    c: Horizontal(g3)
    c: DistanceX(g0) = -30
    c: DistanceX(g1) = 30
    c: DistanceY(g0) = -327
    c: DistanceY(g0,g0) = 50
FEATURE [Sketcher::SketchObject] Sketch029  label="outer010"
  FullyConstrained = true
  Placement = pos=(0,0,-281.2) rot=(0,0,1;0rad)
  sketch-geometry (4):
    g0: LineSegment StartX=-59 StartY=-252 StartZ=0 EndX=-59 EndY=-352 EndZ=0
    g1: LineSegment StartX=-59 StartY=-352 StartZ=0 EndX=59 EndY=-352 EndZ=0
    g2: LineSegment StartX=59 StartY=-352 StartZ=0 EndX=59 EndY=-252 EndZ=0
    g3: LineSegment StartX=59 StartY=-252 StartZ=0 EndX=-59 EndY=-252 EndZ=0
  constraints (12):
    c: Vertical(g0)
    c: Coincident(g1,g0)
    c: Horizontal(g1)
    c: Coincident(g2,g1)
    c: Vertical(g2)
    c: Coincident(g3,g2)
    c: Coincident(g3,g0)
    c: Horizontal(g3)
    c: DistanceX(g0) = -59
    c: DistanceX(g1) = 59
    c: DistanceY(g0) = -352
    c: DistanceY(g0,g0) = 100
FEATURE [Part::Loft] Loft010
  Closed = false
  MaxDegree = 5
  Ruled = false
  Sections = -> [Sketch028,Sketch029]
  Solid = true
FEATURE [Part::Fillet] Fillet018
  Base = -> Loft010
  Edges = 12 edges r=3: [Edge1,Edge2,Edge3,Edge4,Edge5,Edge6,Edge7,Edge8,Edge9,Edge10,Edge11,Edge12]
FEATURE [Sketcher::SketchObject] Sketch030  label="inner011"
  FullyConstrained = true
  Placement = pos=(0,0,-259.26) rot=(0,0,1;0rad)
  sketch-geometry (4):
    g0: LineSegment StartX=-30 StartY=-277 StartZ=0 EndX=-30 EndY=-327 EndZ=0
    g1: LineSegment StartX=-30 StartY=-327 StartZ=0 EndX=30 EndY=-327 EndZ=0
    g2: LineSegment StartX=30 StartY=-327 StartZ=0 EndX=30 EndY=-277 EndZ=0
    g3: LineSegment StartX=30 StartY=-277 StartZ=0 EndX=-30 EndY=-277 EndZ=0
  constraints (12):
    c: Vertical(g0)
    c: Coincident(g1,g0)
    c: Horizontal(g1)
    c: Coincident(g2,g1)
    c: Vertical(g2)
    c: Coincident(g3,g2)
    c: Coincident(g3,g0)
    c: Horizontal(g3)
    c: DistanceX(g0) = -30
    c: DistanceX(g1) = 30
    c: DistanceY(g0) = -327
    c: DistanceY(g0,g0) = 50
FEATURE [Sketcher::SketchObject] Sketch031  label="outer011"
  FullyConstrained = true
  Placement = pos=(0,0,-281.2) rot=(0,0,1;0rad)
  sketch-geometry (4):
    g0: LineSegment StartX=-59 StartY=-252 StartZ=0 EndX=-59 EndY=-352 EndZ=0
    g1: LineSegment StartX=-59 StartY=-352 StartZ=0 EndX=59 EndY=-352 EndZ=0
    g2: LineSegment StartX=59 StartY=-352 StartZ=0 EndX=59 EndY=-252 EndZ=0
    g3: LineSegment StartX=59 StartY=-252 StartZ=0 EndX=-59 EndY=-252 EndZ=0
  constraints (12):
    c: Vertical(g0)
    c: Coincident(g1,g0)
    c: Horizontal(g1)
    c: Coincident(g2,g1)
    c: Vertical(g2)
    c: Coincident(g3,g2)
    c: Coincident(g3,g0)
    c: Horizontal(g3)
    c: DistanceX(g0) = -59
    c: DistanceX(g1) = 59
    c: DistanceY(g0) = -352
    c: DistanceY(g0,g0) = 100
FEATURE [Part::Loft] Loft011
  Closed = false
  MaxDegree = 5
  Ruled = false
  Sections = -> [Sketch030,Sketch031]
  Solid = true
FEATURE [Part::Fillet] Fillet019
  Base = -> Loft011
  Edges = 12 edges r=3: [Edge1,Edge2,Edge3,Edge4,Edge5,Edge6,Edge7,Edge8,Edge9,Edge10,Edge11,Edge12]
  Placement = pos=(0,0,-4) rot=(0,0,1;0rad)
FEATURE [Part::Cut] Cut008  label="sls006"
  Base = -> Fillet018
  Placement = pos=(0,0,7) rot=(0,0,1;0rad)
  Tool = -> Fillet019
FEATURE [Sketcher::SketchObject] Sketch033
  FullyConstrained = true
  Placement = pos=(0,0,0) rot=(1,0,0;1.5708rad)
  sketch-geometry (4):
    g0: LineSegment StartX=-22 StartY=-275.2 StartZ=0 EndX=22 EndY=-275.2 EndZ=0
    g1: LineSegment StartX=22 StartY=-275.2 StartZ=0 EndX=22 EndY=-323.5 EndZ=0
    g2: LineSegment StartX=22 StartY=-323.5 StartZ=0 EndX=-22 EndY=-323.5 EndZ=0
    g3: LineSegment StartX=-22 StartY=-323.5 StartZ=0 EndX=-22 EndY=-275.2 EndZ=0
  constraints (12):
    c: Coincident(g0,g1)
    c: Coincident(g1,g2)
    c: Coincident(g2,g3)
    c: Coincident(g3,g0)
    c: Horizontal(g0)
    c: Horizontal(g2)
    c: Vertical(g1)
    c: Vertical(g3)
    c: DistanceX(g1) = 22
    c: DistanceX(g0) = -22
    c: DistanceY(g0) = -275.2
    c: DistanceY(g2) = -323.5
FEATURE [Part::Extrusion] Extrude009  label="face"
  Base = -> Sketch033
  Dir = (0,-1,2e-16)
  DirMode = 2
  FaceMakerClass = Part::FaceMakerBullseye
  LengthFwd = 2
  LengthRev = 0
  Placement = pos=(0,-325.87,0) rot=(0,0,1;0rad)
  Solid = true
  Symmetric = false
FEATURE [Sketcher::SketchObject] Sketch034
  FullyConstrained = true
  sketch-geometry (4):
    g0: Circle CenterX=-35 CenterY=-332 CenterZ=0 NormalX=0 NormalY=0 NormalZ=1 AngleXU=0 Radius=2
    g1: Circle CenterX=35 CenterY=-332 CenterZ=0 NormalX=0 NormalY=0 NormalZ=1 AngleXU=0 Radius=2
    g2: Circle CenterX=35 CenterY=-272 CenterZ=0 NormalX=0 NormalY=0 NormalZ=1 AngleXU=0 Radius=2
    g3: Circle CenterX=-35 CenterY=-272 CenterZ=0 NormalX=0 NormalY=0 NormalZ=1 AngleXU=0 Radius=2
  constraints (12):
    c: DistanceX(g0) = -35
    c: DistanceY(g0) = -332
    c: Equal(g0,g3)
    c: Equal(g0,g2)
    c: Equal(g0,g1)
    c: Diameter(g0) = 4
    c: DistanceX(g3,g0) = 0
    c: DistanceY(g0,g3) = 60
    c: DistanceY(g2,g3) = 0
    c: DistanceY(g0,g1) = 0
    c: DistanceX(g2,g1) = 0
    c: DistanceX(g1) = 35
FEATURE [Part::Extrusion] Extrude010  label="slsCuts"
  Base = -> Sketch034
  Dir = (0,0,1)
  DirMode = 2
  FaceMakerClass = Part::FaceMakerBullseye
  LengthFwd = 20
  LengthRev = 0
  Placement = pos=(0,0,-323) rot=(0,0,1;0rad)
  Solid = true
  Symmetric = false
FEATURE [Part::MultiFuse] Fusion036  label="slsBottom"
  Shapes = -> [Cut006,Cut005]
FEATURE [Sketcher::SketchObject] Sketch036
  FullyConstrained = true
  MapMode = 2
  sketch-geometry (4):
    g0: LineSegment StartX=-28 StartY=-347.85 StartZ=0 EndX=28 EndY=-347.85 EndZ=0
    g1: LineSegment StartX=18 StartY=-327.85 StartZ=0 EndX=28 EndY=-347.85 EndZ=0
    g2: LineSegment StartX=-28 StartY=-347.85 StartZ=0 EndX=-18 EndY=-327.85 EndZ=0
    g3: LineSegment StartX=-18 StartY=-327.85 StartZ=0 EndX=18 EndY=-327.85 EndZ=0
  constraints (12):
    c: Horizontal(g0)
    c: Coincident(g1,g0)
    c: Coincident(g2,g0)
    c: Coincident(g3,g2)
    c: Coincident(g3,g1)
    c: Horizontal(g3)
    c: DistanceX(g2) = -18
    c: DistanceX(g1) = 18
    c: DistanceX(g0,g2) = 10
    c: DistanceY(g2) = -327.85
    c: DistanceY(g0,g2) = 20
    c: DistanceX(g1,g0) = 10
FEATURE [Part::Extrusion] Extrude012
  Base = -> Sketch036
  Dir = (0,0,1)
  DirMode = 2
  FaceMakerClass = Part::FaceMakerBullseye
  LengthFwd = 40
  LengthRev = 0
  Placement = pos=(0,0,-329) rot=(0,0,1;0rad)
  Solid = true
  Symmetric = false
FEATURE [Part::Cut] Cut011  label="slsBottom001"
  Base = -> Fusion036
  Tool = -> Extrude012
FEATURE [Sketcher::SketchObject] Sketch037
  FullyConstrained = true
  sketch-geometry (4):
    g0: LineSegment StartX=-29 StartY=-278.2 StartZ=0 EndX=29 EndY=-278.2 EndZ=0
    g1: LineSegment StartX=29 StartY=-278.2 StartZ=0 EndX=29 EndY=-325.8 EndZ=0
    g2: LineSegment StartX=29 StartY=-325.8 StartZ=0 EndX=-29 EndY=-325.8 EndZ=0
    g3: LineSegment StartX=-29 StartY=-325.8 StartZ=0 EndX=-29 EndY=-278.2 EndZ=0
  constraints (12):
    c: Coincident(g0,g1)
    c: Coincident(g1,g2)
    c: Coincident(g2,g3)
    c: Coincident(g3,g0)
    c: Horizontal(g0)
    c: Horizontal(g2)
    c: Vertical(g1)
    c: Vertical(g3)
    c: DistanceX(g2) = -29
    c: DistanceY(g2) = -325.8
    c: DistanceY(g2,g0) = 47.6
    c: DistanceX(g1) = 29
FEATURE [Part::Extrusion] Extrude013  label="slsCut"
  Base = -> Sketch037
  Dir = (0,0,1)
  DirMode = 2
  FaceMakerClass = Part::FaceMakerBullseye
  LengthFwd = 60
  LengthRev = 0
  Placement = pos=(0,0,-329) rot=(0,0,1;0rad)
  Solid = true
  Symmetric = false
FEATURE [Part::MultiFuse] Fusion037  label="sls"
  Shapes = -> [Cut011,Extrude009,Extrude007,Cut004,Cut]
FEATURE [Part::Cut] Cut012  label="sls007"
  Base = -> Fusion037
  Tool = -> Extrude013
FEATURE [Sketcher::SketchObject] Sketch038  label="inner012"
  FullyConstrained = true
  Placement = pos=(0,0,-259.26) rot=(0,0,1;0rad)
  sketch-geometry (4):
    g0: LineSegment StartX=-30 StartY=-277 StartZ=0 EndX=-30 EndY=-327 EndZ=0
    g1: LineSegment StartX=-30 StartY=-327 StartZ=0 EndX=30 EndY=-327 EndZ=0
    g2: LineSegment StartX=30 StartY=-327 StartZ=0 EndX=30 EndY=-277 EndZ=0
    g3: LineSegment StartX=30 StartY=-277 StartZ=0 EndX=-30 EndY=-277 EndZ=0
  constraints (12):
    c: Vertical(g0)
    c: Coincident(g1,g0)
    c: Horizontal(g1)
    c: Coincident(g2,g1)
    c: Vertical(g2)
    c: Coincident(g3,g2)
    c: Coincident(g3,g0)
    c: Horizontal(g3)
    c: DistanceX(g0) = -30
    c: DistanceX(g1) = 30
    c: DistanceY(g0) = -327
    c: DistanceY(g0,g0) = 50
FEATURE [Sketcher::SketchObject] Sketch039  label="outer012"
  FullyConstrained = true
  Placement = pos=(0,0,-281.2) rot=(0,0,1;0rad)
  sketch-geometry (4):
    g0: LineSegment StartX=-59 StartY=-252 StartZ=0 EndX=-59 EndY=-352 EndZ=0
    g1: LineSegment StartX=-59 StartY=-352 StartZ=0 EndX=59 EndY=-352 EndZ=0
    g2: LineSegment StartX=59 StartY=-352 StartZ=0 EndX=59 EndY=-252 EndZ=0
    g3: LineSegment StartX=59 StartY=-252 StartZ=0 EndX=-59 EndY=-252 EndZ=0
  constraints (12):
    c: Vertical(g0)
    c: Coincident(g1,g0)
    c: Horizontal(g1)
    c: Coincident(g2,g1)
    c: Vertical(g2)
    c: Coincident(g3,g2)
    c: Coincident(g3,g0)
    c: Horizontal(g3)
    c: DistanceX(g0) = -59
    c: DistanceX(g1) = 59
    c: DistanceY(g0) = -352
    c: DistanceY(g0,g0) = 100
FEATURE [Part::Loft] Loft012
  Closed = false
  MaxDegree = 5
  Ruled = false
  Sections = -> [Sketch038,Sketch039]
  Solid = true
FEATURE [Part::Fillet] Fillet020
  Base = -> Loft012
  Edges = 12 edges r=3: [Edge1,Edge2,Edge3,Edge4,Edge5,Edge6,Edge7,Edge8,Edge9,Edge10,Edge11,Edge12]
FEATURE [Sketcher::SketchObject] Sketch040  label="inner013"
  FullyConstrained = true
  Placement = pos=(0,0,-259.26) rot=(0,0,1;0rad)
  sketch-geometry (4):
    g0: LineSegment StartX=-30 StartY=-277 StartZ=0 EndX=-30 EndY=-327 EndZ=0
    g1: LineSegment StartX=-30 StartY=-327 StartZ=0 EndX=30 EndY=-327 EndZ=0
    g2: LineSegment StartX=30 StartY=-327 StartZ=0 EndX=30 EndY=-277 EndZ=0
    g3: LineSegment StartX=30 StartY=-277 StartZ=0 EndX=-30 EndY=-277 EndZ=0
  constraints (12):
    c: Vertical(g0)
    c: Coincident(g1,g0)
    c: Horizontal(g1)
    c: Coincident(g2,g1)
    c: Vertical(g2)
    c: Coincident(g3,g2)
    c: Coincident(g3,g0)
    c: Horizontal(g3)
    c: DistanceX(g0) = -30
    c: DistanceX(g1) = 30
    c: DistanceY(g0) = -327
    c: DistanceY(g0,g0) = 50
FEATURE [Sketcher::SketchObject] Sketch041  label="outer013"
  FullyConstrained = true
  Placement = pos=(0,0,-281.2) rot=(0,0,1;0rad)
  sketch-geometry (4):
    g0: LineSegment StartX=-59 StartY=-252 StartZ=0 EndX=-59 EndY=-352 EndZ=0
    g1: LineSegment StartX=-59 StartY=-352 StartZ=0 EndX=59 EndY=-352 EndZ=0
    g2: LineSegment StartX=59 StartY=-352 StartZ=0 EndX=59 EndY=-252 EndZ=0
    g3: LineSegment StartX=59 StartY=-252 StartZ=0 EndX=-59 EndY=-252 EndZ=0
  constraints (12):
    c: Vertical(g0)
    c: Coincident(g1,g0)
    c: Horizontal(g1)
    c: Coincident(g2,g1)
    c: Vertical(g2)
    c: Coincident(g3,g2)
    c: Coincident(g3,g0)
    c: Horizontal(g3)
    c: DistanceX(g0) = -59
    c: DistanceX(g1) = 59
    c: DistanceY(g0) = -352
    c: DistanceY(g0,g0) = 100
FEATURE [Part::Loft] Loft013
  Closed = false
  MaxDegree = 5
  Ruled = false
  Sections = -> [Sketch040,Sketch041]
  Solid = true
FEATURE [Part::Fillet] Fillet021
  Base = -> Loft013
  Edges = 12 edges r=3: [Edge1,Edge2,Edge3,Edge4,Edge5,Edge6,Edge7,Edge8,Edge9,Edge10,Edge11,Edge12]
  Placement = pos=(0,0,-4) rot=(0,0,1;0rad)
FEATURE [Part::Cut] Cut013  label="sls008"
  Base = -> Fillet020
  Placement = pos=(0,0,10) rot=(0,0,1;0rad)
  Tool = -> Fillet021
FEATURE [Part::MultiFuse] Fusion039
  Shapes = -> [Cut013,Cut008,Cut007]
FEATURE [Sketcher::SketchObject] Sketch042  label="inner014"
  FullyConstrained = true
  Placement = pos=(0,0,-259.26) rot=(0,0,1;0rad)
  sketch-geometry (4):
    g0: LineSegment StartX=-30 StartY=-277 StartZ=0 EndX=-30 EndY=-327 EndZ=0
    g1: LineSegment StartX=-30 StartY=-327 StartZ=0 EndX=30 EndY=-327 EndZ=0
    g2: LineSegment StartX=30 StartY=-327 StartZ=0 EndX=30 EndY=-277 EndZ=0
    g3: LineSegment StartX=30 StartY=-277 StartZ=0 EndX=-30 EndY=-277 EndZ=0
  constraints (12):
    c: Vertical(g0)
    c: Coincident(g1,g0)
    c: Horizontal(g1)
    c: Coincident(g2,g1)
    c: Vertical(g2)
    c: Coincident(g3,g2)
    c: Coincident(g3,g0)
    c: Horizontal(g3)
    c: DistanceX(g0) = -30
    c: DistanceX(g1) = 30
    c: DistanceY(g0) = -327
    c: DistanceY(g0,g0) = 50
FEATURE [Sketcher::SketchObject] Sketch043  label="outer014"
  FullyConstrained = true
  Placement = pos=(0,0,-281.2) rot=(0,0,1;0rad)
  sketch-geometry (4):
    g0: LineSegment StartX=-59 StartY=-252 StartZ=0 EndX=-59 EndY=-352 EndZ=0
    g1: LineSegment StartX=-59 StartY=-352 StartZ=0 EndX=59 EndY=-352 EndZ=0
    g2: LineSegment StartX=59 StartY=-352 StartZ=0 EndX=59 EndY=-252 EndZ=0
    g3: LineSegment StartX=59 StartY=-252 StartZ=0 EndX=-59 EndY=-252 EndZ=0
  constraints (12):
    c: Vertical(g0)
    c: Coincident(g1,g0)
    c: Horizontal(g1)
    c: Coincident(g2,g1)
    c: Vertical(g2)
    c: Coincident(g3,g2)
    c: Coincident(g3,g0)
    c: Horizontal(g3)
    c: DistanceX(g0) = -59
    c: DistanceX(g1) = 59
    c: DistanceY(g0) = -352
    c: DistanceY(g0,g0) = 100
FEATURE [Part::Loft] Loft014
  Closed = false
  MaxDegree = 5
  Ruled = false
  Sections = -> [Sketch042,Sketch043]
  Solid = true
FEATURE [Part::Fillet] Fillet022
  Base = -> Loft014
  Edges = 12 edges r=3: [Edge1,Edge2,Edge3,Edge4,Edge5,Edge6,Edge7,Edge8,Edge9,Edge10,Edge11,Edge12]
FEATURE [Sketcher::SketchObject] Sketch044  label="inner015"
  FullyConstrained = true
  Placement = pos=(0,0,-259.26) rot=(0,0,1;0rad)
  sketch-geometry (4):
    g0: LineSegment StartX=-36 StartY=-277 StartZ=0 EndX=-36 EndY=-327 EndZ=0
    g1: LineSegment StartX=-36 StartY=-327 StartZ=0 EndX=36 EndY=-327 EndZ=0
    g2: LineSegment StartX=36 StartY=-327 StartZ=0 EndX=36 EndY=-277 EndZ=0
    g3: LineSegment StartX=36 StartY=-277 StartZ=0 EndX=-36 EndY=-277 EndZ=0
  constraints (12):
    c: Vertical(g0)
    c: Coincident(g1,g0)
    c: Horizontal(g1)
    c: Coincident(g2,g1)
    c: Vertical(g2)
    c: Coincident(g3,g2)
    c: Coincident(g3,g0)
    c: Horizontal(g3)
    c: DistanceX(g0) = -36
    c: DistanceX(g1) = 36
    c: DistanceY(g0) = -327
    c: DistanceY(g0,g0) = 50
FEATURE [Sketcher::SketchObject] Sketch045  label="outer015"
  FullyConstrained = true
  Placement = pos=(0,0,-281.2) rot=(0,0,1;0rad)
  sketch-geometry (4):
    g0: LineSegment StartX=-65 StartY=-252 StartZ=0 EndX=-65 EndY=-352 EndZ=0
    g1: LineSegment StartX=-65 StartY=-352 StartZ=0 EndX=65 EndY=-352 EndZ=0
    g2: LineSegment StartX=65 StartY=-352 StartZ=0 EndX=65 EndY=-252 EndZ=0
    g3: LineSegment StartX=65 StartY=-252 StartZ=0 EndX=-65 EndY=-252 EndZ=0
  constraints (12):
    c: Vertical(g0)
    c: Coincident(g1,g0)
    c: Horizontal(g1)
    c: Coincident(g2,g1)
    c: Vertical(g2)
    c: Coincident(g3,g2)
    c: Coincident(g3,g0)
    c: Horizontal(g3)
    c: DistanceX(g0) = -65
    c: DistanceX(g1) = 65
    c: DistanceY(g0) = -352
    c: DistanceY(g0,g0) = 100
FEATURE [Part::Loft] Loft015
  Closed = false
  MaxDegree = 5
  Ruled = false
  Sections = -> [Sketch044,Sketch045]
  Solid = true
FEATURE [Part::Fillet] Fillet023
  Base = -> Loft015
  Edges = 12 edges r=3: [Edge1,Edge2,Edge3,Edge4,Edge5,Edge6,Edge7,Edge8,Edge9,Edge10,Edge11,Edge12]
  Placement = pos=(0,0,-4) rot=(0,0,1;0rad)
FEATURE [Part::Cut] Cut014  label="sls009"
  Base = -> Fillet022
  Placement = pos=(0,0,4) rot=(0,0,1;0rad)
  Tool = -> Fillet023
FEATURE [Sketcher::SketchObject] Sketch046  label="inner016"
  FullyConstrained = true
  Placement = pos=(0,0,-259.26) rot=(0,0,1;0rad)
  sketch-geometry (4):
    g0: LineSegment StartX=-30 StartY=-277 StartZ=0 EndX=-30 EndY=-327 EndZ=0
    g1: LineSegment StartX=-30 StartY=-327 StartZ=0 EndX=30 EndY=-327 EndZ=0
    g2: LineSegment StartX=30 StartY=-327 StartZ=0 EndX=30 EndY=-277 EndZ=0
    g3: LineSegment StartX=30 StartY=-277 StartZ=0 EndX=-30 EndY=-277 EndZ=0
  constraints (12):
    c: Vertical(g0)
    c: Coincident(g1,g0)
    c: Horizontal(g1)
    c: Coincident(g2,g1)
    c: Vertical(g2)
    c: Coincident(g3,g2)
    c: Coincident(g3,g0)
    c: Horizontal(g3)
    c: DistanceX(g0) = -30
    c: DistanceX(g1) = 30
    c: DistanceY(g0) = -327
    c: DistanceY(g0,g0) = 50
FEATURE [Sketcher::SketchObject] Sketch047  label="outer016"
  FullyConstrained = true
  Placement = pos=(0,0,-281.2) rot=(0,0,1;0rad)
  sketch-geometry (4):
    g0: LineSegment StartX=-59 StartY=-252 StartZ=0 EndX=-59 EndY=-352 EndZ=0
    g1: LineSegment StartX=-59 StartY=-352 StartZ=0 EndX=59 EndY=-352 EndZ=0
    g2: LineSegment StartX=59 StartY=-352 StartZ=0 EndX=59 EndY=-252 EndZ=0
    g3: LineSegment StartX=59 StartY=-252 StartZ=0 EndX=-59 EndY=-252 EndZ=0
  constraints (12):
    c: Vertical(g0)
    c: Coincident(g1,g0)
    c: Horizontal(g1)
    c: Coincident(g2,g1)
    c: Vertical(g2)
    c: Coincident(g3,g2)
    c: Coincident(g3,g0)
    c: Horizontal(g3)
    c: DistanceX(g0) = -59
    c: DistanceX(g1) = 59
    c: DistanceY(g0) = -352
    c: DistanceY(g0,g0) = 100
FEATURE [Part::Loft] Loft016
  Closed = false
  MaxDegree = 5
  Ruled = false
  Sections = -> [Sketch046,Sketch047]
  Solid = true
FEATURE [Part::Fillet] Fillet024
  Base = -> Loft016
  Edges = 12 edges r=3: [Edge1,Edge2,Edge3,Edge4,Edge5,Edge6,Edge7,Edge8,Edge9,Edge10,Edge11,Edge12]
FEATURE [Sketcher::SketchObject] Sketch048  label="inner017"
  FullyConstrained = true
  Placement = pos=(0,0,-259.26) rot=(0,0,1;0rad)
  sketch-geometry (4):
    g0: LineSegment StartX=-30 StartY=-277 StartZ=0 EndX=-30 EndY=-327 EndZ=0
    g1: LineSegment StartX=-30 StartY=-327 StartZ=0 EndX=30 EndY=-327 EndZ=0
    g2: LineSegment StartX=30 StartY=-327 StartZ=0 EndX=30 EndY=-277 EndZ=0
    g3: LineSegment StartX=30 StartY=-277 StartZ=0 EndX=-30 EndY=-277 EndZ=0
  constraints (12):
    c: Vertical(g0)
    c: Coincident(g1,g0)
    c: Horizontal(g1)
    c: Coincident(g2,g1)
    c: Vertical(g2)
    c: Coincident(g3,g2)
    c: Coincident(g3,g0)
    c: Horizontal(g3)
    c: DistanceX(g0) = -30
    c: DistanceX(g1) = 30
    c: DistanceY(g0) = -327
    c: DistanceY(g0,g0) = 50
FEATURE [Sketcher::SketchObject] Sketch049  label="outer017"
  FullyConstrained = true
  Placement = pos=(0,0,-281.2) rot=(0,0,1;0rad)
  sketch-geometry (4):
    g0: LineSegment StartX=-65 StartY=-252 StartZ=0 EndX=-65 EndY=-352 EndZ=0
    g1: LineSegment StartX=-65 StartY=-352 StartZ=0 EndX=65 EndY=-352 EndZ=0
    g2: LineSegment StartX=65 StartY=-352 StartZ=0 EndX=65 EndY=-252 EndZ=0
    g3: LineSegment StartX=65 StartY=-252 StartZ=0 EndX=-65 EndY=-252 EndZ=0
  constraints (12):
    c: Vertical(g0)
    c: Coincident(g1,g0)
    c: Horizontal(g1)
    c: Coincident(g2,g1)
    c: Vertical(g2)
    c: Coincident(g3,g2)
    c: Coincident(g3,g0)
    c: Horizontal(g3)
    c: DistanceX(g0) = -65
    c: DistanceX(g1) = 65
    c: DistanceY(g0) = -352
    c: DistanceY(g0,g0) = 100
FEATURE [Part::Loft] Loft017
  Closed = false
  MaxDegree = 5
  Ruled = false
  Sections = -> [Sketch048,Sketch049]
  Solid = true
FEATURE [Part::Fillet] Fillet025
  Base = -> Loft017
  Edges = 12 edges r=3: [Edge1,Edge2,Edge3,Edge4,Edge5,Edge6,Edge7,Edge8,Edge9,Edge10,Edge11,Edge12]
  Placement = pos=(0,0,-4) rot=(0,0,1;0rad)
FEATURE [Part::Cut] Cut015  label="sls010"
  Base = -> Fillet024
  Placement = pos=(0,0,7) rot=(0,0,1;0rad)
  Tool = -> Fillet025
FEATURE [Sketcher::SketchObject] Sketch050  label="inner018"
  FullyConstrained = true
  Placement = pos=(0,0,-259.26) rot=(0,0,1;0rad)
  sketch-geometry (4):
    g0: LineSegment StartX=-30 StartY=-277 StartZ=0 EndX=-30 EndY=-327 EndZ=0
    g1: LineSegment StartX=-30 StartY=-327 StartZ=0 EndX=30 EndY=-327 EndZ=0
    g2: LineSegment StartX=30 StartY=-327 StartZ=0 EndX=30 EndY=-277 EndZ=0
    g3: LineSegment StartX=30 StartY=-277 StartZ=0 EndX=-30 EndY=-277 EndZ=0
  constraints (12):
    c: Vertical(g0)
    c: Coincident(g1,g0)
    c: Horizontal(g1)
    c: Coincident(g2,g1)
    c: Vertical(g2)
    c: Coincident(g3,g2)
    c: Coincident(g3,g0)
    c: Horizontal(g3)
    c: DistanceX(g0) = -30
    c: DistanceX(g1) = 30
    c: DistanceY(g0) = -327
    c: DistanceY(g0,g0) = 50
FEATURE [Sketcher::SketchObject] Sketch051  label="outer018"
  FullyConstrained = true
  Placement = pos=(0,0,-281.2) rot=(0,0,1;0rad)
  sketch-geometry (4):
    g0: LineSegment StartX=-59 StartY=-252 StartZ=0 EndX=-59 EndY=-352 EndZ=0
    g1: LineSegment StartX=-59 StartY=-352 StartZ=0 EndX=59 EndY=-352 EndZ=0
    g2: LineSegment StartX=59 StartY=-352 StartZ=0 EndX=59 EndY=-252 EndZ=0
    g3: LineSegment StartX=59 StartY=-252 StartZ=0 EndX=-59 EndY=-252 EndZ=0
  constraints (12):
    c: Vertical(g0)
    c: Coincident(g1,g0)
    c: Horizontal(g1)
    c: Coincident(g2,g1)
    c: Vertical(g2)
    c: Coincident(g3,g2)
    c: Coincident(g3,g0)
    c: Horizontal(g3)
    c: DistanceX(g0) = -59
    c: DistanceX(g1) = 59
    c: DistanceY(g0) = -352
    c: DistanceY(g0,g0) = 100
FEATURE [Part::Loft] Loft018
  Closed = false
  MaxDegree = 5
  Ruled = false
  Sections = -> [Sketch050,Sketch051]
  Solid = true
FEATURE [Part::Fillet] Fillet026
  Base = -> Loft018
  Edges = 12 edges r=3: [Edge1,Edge2,Edge3,Edge4,Edge5,Edge6,Edge7,Edge8,Edge9,Edge10,Edge11,Edge12]
FEATURE [Sketcher::SketchObject] Sketch052  label="inner019"
  FullyConstrained = true
  Placement = pos=(0,0,-259.26) rot=(0,0,1;0rad)
  sketch-geometry (4):
    g0: LineSegment StartX=-30 StartY=-277 StartZ=0 EndX=-30 EndY=-327 EndZ=0
    g1: LineSegment StartX=-30 StartY=-327 StartZ=0 EndX=30 EndY=-327 EndZ=0
    g2: LineSegment StartX=30 StartY=-327 StartZ=0 EndX=30 EndY=-277 EndZ=0
    g3: LineSegment StartX=30 StartY=-277 StartZ=0 EndX=-30 EndY=-277 EndZ=0
  constraints (12):
    c: Vertical(g0)
    c: Coincident(g1,g0)
    c: Horizontal(g1)
    c: Coincident(g2,g1)
    c: Vertical(g2)
    c: Coincident(g3,g2)
    c: Coincident(g3,g0)
    c: Horizontal(g3)
    c: DistanceX(g0) = -30
    c: DistanceX(g1) = 30
    c: DistanceY(g0) = -327
    c: DistanceY(g0,g0) = 50
FEATURE [Sketcher::SketchObject] Sketch053  label="outer019"
  FullyConstrained = true
  Placement = pos=(0,0,-281.2) rot=(0,0,1;0rad)
  sketch-geometry (4):
    g0: LineSegment StartX=-59 StartY=-252 StartZ=0 EndX=-59 EndY=-352 EndZ=0
    g1: LineSegment StartX=-59 StartY=-352 StartZ=0 EndX=59 EndY=-352 EndZ=0
    g2: LineSegment StartX=59 StartY=-352 StartZ=0 EndX=59 EndY=-252 EndZ=0
    g3: LineSegment StartX=59 StartY=-252 StartZ=0 EndX=-59 EndY=-252 EndZ=0
  constraints (12):
    c: Vertical(g0)
    c: Coincident(g1,g0)
    c: Horizontal(g1)
    c: Coincident(g2,g1)
    c: Vertical(g2)
    c: Coincident(g3,g2)
    c: Coincident(g3,g0)
    c: Horizontal(g3)
    c: DistanceX(g0) = -59
    c: DistanceX(g1) = 59
    c: DistanceY(g0) = -352
    c: DistanceY(g0,g0) = 100
FEATURE [Part::Loft] Loft019
  Closed = false
  MaxDegree = 5
  Ruled = false
  Sections = -> [Sketch052,Sketch053]
  Solid = true
FEATURE [Part::Fillet] Fillet027
  Base = -> Loft019
  Edges = 12 edges r=3: [Edge1,Edge2,Edge3,Edge4,Edge5,Edge6,Edge7,Edge8,Edge9,Edge10,Edge11,Edge12]
  Placement = pos=(0,0,-4) rot=(0,0,1;0rad)
FEATURE [Part::Cut] Cut016  label="sls011"
  Base = -> Fillet026
  Placement = pos=(0,0,10) rot=(0,0,1;0rad)
  Tool = -> Fillet027
FEATURE [Part::MultiFuse] Fusion040
  Placement = pos=(0,0,5) rot=(0,0,1;0rad)
  Shapes = -> [Cut016,Cut015,Cut014]
FEATURE [Part::MultiFuse] Fusion041  label="slsCUts"
  Shapes = -> [Fusion040,Fusion039]
FEATURE [Part::MultiFuse] Fusion042  label="slsCuts001"
  Shapes = -> [Fusion041,Extrude010]
FEATURE [Part::Cut] Cut017  label="sls012"
  Base = -> Cut012
  Tool = -> Fusion042
FEATURE [Part::Cut] Cut018  label="sls013"
  Base = -> Cut017
  Placement = pos=(0,17,15) rot=(0,0,1;0rad)
  Tool = -> Part__Feature153
FEATURE [Sketcher::SketchObject] Sketch054
  FullyConstrained = true
  MapMode = 2
  Placement = pos=(-0.5,-512,-305.5) rot=(0.57735,-0.57735,-0.57735;2.0944rad)
  Support = -> [Compound002]
  sketch-geometry (8):
    g0: LineSegment StartX=-225.068 StartY=76.4427 StartZ=0 EndX=-228.265 EndY=72.5985 EndZ=0
    g1: LineSegment StartX=-228.265 StartY=72.5985 StartZ=0 EndX=-209.044 EndY=56.6125 EndZ=0
    g2: LineSegment StartX=-185 StartY=46.25 StartZ=0 EndX=-212.066 EndY=69.9864 EndZ=0
    g3: LineSegment StartX=-214.208 StartY=67.4108 StartZ=0 EndX=-212.066 EndY=69.9864 EndZ=0
    g4: LineSegment StartX=-214.208 StartY=67.4108 StartZ=0 EndX=-225.068 EndY=76.4427 EndZ=0
    g5: LineSegment StartX=-185 StartY=46.25 StartZ=0 EndX=-185 EndY=40.7882 EndZ=0
    g6: LineSegment StartX=-185 StartY=40.7882 StartZ=0 EndX=-203.044 EndY=56.6125 EndZ=0
    g7: LineSegment StartX=-203.044 StartY=56.6125 StartZ=0 EndX=-209.044 EndY=56.6125 EndZ=0
  constraints (24):
    c: Coincident(g0,g1)
    c: Coincident(g2,g3)
    c: Coincident(g4,g3)
    c: Coincident(g4,g0)
    c: Coincident(g5,g2)
    c: Coincident(g6,g5)
    c: Coincident(g7,g6)
    c: Horizontal(g7)
    c: Coincident(g1,g7)
    c: Parallel(g2,g6)
    c: Angle(g3,g2) = 1.54462
    c: Angle(g0,g4) = 1.5708
    c: Angle(g3,g4) = 1.5708
    c: DistanceX(g2) = -185
    c: DistanceY(g2) = 46.25
    c: Vertical(g5)
    c: Angle(g2,g5) = 2.29074
    c: Distance(g2) = 36
    c: Distance(g3) = 3.35
    c: Distance(g0) = 5
    c: Parallel(g4,g1)
    c: DistanceX(g7,g7) = 6
    c: Distance(g1) = 25
    c: Distance(g6) = 24
FEATURE [Part::Extrusion] Extrude014
  Base = -> Sketch054
  Dir = (-1,0,0)
  DirMode = 2
  FaceMakerClass = Part::FaceMakerBullseye
  LengthFwd = 61.6
  LengthRev = 0
  Placement = pos=(31.3,0,0) rot=(0,0,1;0rad)
  Solid = true
  Symmetric = false
FEATURE [Part::Cylinder] Cylinder
  Angle = 360
  AttacherType = Attacher::AttachEngine3D
  FirstAngle = 0
  Height = 15
  Placement = pos=(0,-287.79,-241.35) rot=(1,0,0;0.698132rad)
  Radius = 1.63
  SecondAngle = 0
FEATURE [Part::Cut] Cut020
  Base = -> Extrude014
  Tool = -> Cylinder
FEATURE [Part::MultiFuse] Fusion043  label="sls014"
  Shapes = -> [Cut020,Cut018]
FEATURE [Part::Feature] Part__Feature154  label="Body"
  shape: bbox 15.5 x 16.75 x 29 mm, 21 faces (baked)
FEATURE [Part::Feature] Part__Feature155  label="Body001"
  Placement = pos=(0,0,2) rot=(0,0,1;0rad)
  shape: bbox 17.44 x 17.44 x 14.25 mm, 14 faces (baked)
FEATURE [Part::Feature] Part__Feature156  label="Body002"
  Placement = pos=(0,0,-2.9) rot=(0,0,1;0rad)
  shape: bbox 19 x 19 x 4.75 mm, 25 faces (baked)
FEATURE [Part::Feature] Part__Feature157  label="Body003"
  shape: bbox 16.75 x 16.75 x 0.9 mm, 4 faces (baked)
FEATURE [App::Part] PG7_Gland1
  Group = -> [Part__Feature154,Part__Feature155,Part__Feature156,Part__Feature157]
  Origin = -> Origin017
  Placement = pos=(36,-274,-311.5) rot=(0,1,0;3.14159rad)
FEATURE [Part::Cone] Cone
  Angle = 360
  AttacherType = Attacher::AttachEngine3D
  Height = 1.5
  Placement = pos=(0,0,25.5) rot=(0,0,1;0rad)
  Radius1 = 4
  Radius2 = 3.5
FEATURE [Part::Cylinder] Cylinder020
  Angle = 360
  AttacherType = Attacher::AttachEngine3D
  FirstAngle = 0
  Height = 22
  Placement = pos=(0,0,5) rot=(0,0,1;0rad)
  Radius = 3.2
  SecondAngle = 0
FEATURE [Part::Cylinder] Cylinder021
  Angle = 360
  AttacherType = Attacher::AttachEngine3D
  FirstAngle = 0
  Height = 2
  Placement = pos=(0,0,5) rot=(0,0,1;0rad)
  Radius = 3.55
  SecondAngle = 0
FEATURE [Part::Cylinder] Cylinder022
  Angle = 360
  AttacherType = Attacher::AttachEngine3D
  FirstAngle = 0
  Height = 1
  Placement = pos=(0,0,11) rot=(0,0,1;0rad)
  Radius = 3.55
  SecondAngle = 0
FEATURE [Part::Cylinder] Cylinder023
  Angle = 360
  AttacherType = Attacher::AttachEngine3D
  FirstAngle = 0
  Height = 8
  Placement = pos=(0,0,12) rot=(0,0,1;0rad)
  Radius = 3.25
  SecondAngle = 0
FEATURE [Part::Cylinder] Cylinder024
  Angle = 360
  AttacherType = Attacher::AttachEngine3D
  FirstAngle = 0
  Height = 5.5
  Placement = pos=(0,0,20) rot=(0,0,1;0rad)
  Radius = 4
  SecondAngle = 0
FEATURE [Part::Cylinder] Cylinder025
  Angle = 360
  AttacherType = Attacher::AttachEngine3D
  FirstAngle = 0
  Height = 2
  Placement = pos=(0,0,3) rot=(0,0,1;0rad)
  Radius = 1
  SecondAngle = 0
FEATURE [Part::MultiFuse] Fusion002
  Shapes = -> [Cone,Cylinder020,Cylinder021,Cylinder022,Cylinder023,Cylinder024]
FEATURE [Part::MultiFuse] Fusion044  label="mic"
  Placement = pos=(0,-288.5,-302.5) rot=(0,1,0;3.14159rad)
  Shapes = -> [Cylinder025,Fusion002]
FEATURE [Part::Feature] Part__Feature162  label="Body007"
  shape: bbox 15.5 x 16.75 x 29 mm, 21 faces (baked)
FEATURE [Part::Feature] Part__Feature163  label="Body008"
  Placement = pos=(0,0,2) rot=(0,0,1;0rad)
  shape: bbox 17.44 x 17.44 x 14.25 mm, 14 faces (baked)
FEATURE [Part::Feature] Part__Feature164  label="Body009"
  Placement = pos=(0,0,-2.9) rot=(0,0,1;0rad)
  shape: bbox 19 x 19 x 4.75 mm, 25 faces (baked)
FEATURE [Part::Feature] Part__Feature165  label="Body010"
  shape: bbox 16.75 x 16.75 x 0.9 mm, 4 faces (baked)
FEATURE [App::Part] PG7_Gland002
  Group = -> [Part__Feature162,Part__Feature163,Part__Feature164,Part__Feature165]
  Origin = -> Origin019
  Placement = pos=(-36,-274,-311.5) rot=(0,1,0;3.14159rad)
FEATURE [Part::Extrusion] Extrude005  label="ipsHold"
  Base = -> Sketch021
  Dir = (0,-1,2e-16)
  DirMode = 2
  FaceMakerClass = Part::FaceMakerBullseye
  LengthFwd = 5
  LengthRev = 0
  Placement = pos=(0,-262.5,0) rot=(0,0,1;0rad)
  Solid = true
  Symmetric = false
FEATURE [Sketcher::SketchObject] Sketch093  label="base010"
  FullyConstrained = false
  sketch-geometry (14):
    g0: LineSegment StartX=-41 StartY=-249 StartZ=0 EndX=41 EndY=-249 EndZ=0
    g1: LineSegment StartX=41 StartY=-249 StartZ=0 EndX=41 EndY=-321 EndZ=0
    g2: LineSegment StartX=41 StartY=-321 StartZ=0 EndX=-41 EndY=-321 EndZ=0
    g3: LineSegment StartX=-41 StartY=-249 StartZ=0 EndX=-41 EndY=-321 EndZ=0
    g4: Circle CenterX=-35 CenterY=-315 CenterZ=0 NormalX=0 NormalY=0 NormalZ=1 AngleXU=0 Radius=1.625
    g5: Circle CenterX=35 CenterY=-315 CenterZ=0 NormalX=0 NormalY=0 NormalZ=1 AngleXU=0 Radius=1.625
    g6: Circle CenterX=35 CenterY=-255 CenterZ=0 NormalX=0 NormalY=0 NormalZ=1 AngleXU=0 Radius=1.625
    g7: Circle CenterX=-35 CenterY=-255 CenterZ=0 NormalX=0 NormalY=0 NormalZ=1 AngleXU=0 Radius=1.625
    g8: ArcOfCircle CenterX=-7.5 CenterY=-288.5 CenterZ=0 NormalX=0 NormalY=0 NormalZ=1 AngleXU=0 Radius=5 StartAngle=0.694498 EndAngle=5.58869
    g9: ArcOfCircle CenterX=0 CenterY=-288.5 CenterZ=0 NormalX=0 NormalY=0 NormalZ=1 AngleXU=0 Radius=3.2 StartAngle=4.58731 EndAngle=7.97906
    g10: LineSegment StartX=-0.399218 StartY=-291.675 StartZ=0 EndX=-3.65813 EndY=-291.7 EndZ=0
    g11: LineSegment StartX=-0.399218 StartY=-285.325 StartZ=0 EndX=-3.65813 EndY=-285.3 EndZ=0
    g12: ArcOfCircle CenterX=-2.15519 CenterY=-255.282 CenterZ=0 NormalX=0 NormalY=0 NormalZ=1 AngleXU=0 Radius=2.04125 StartAngle=2.56729 EndAngle=4.95737
    g13: ArcOfCircle CenterX=2.48208 CenterY=-254.879 CenterZ=0 NormalX=0 NormalY=0 NormalZ=1 AngleXU=0 Radius=2.62881 StartAngle=4.84792 EndAngle=7.93075
  constraints (38):
    c: Coincident(g0,g1)
    c: Coincident(g1,g2)
    c: Horizontal(g0)
    c: Horizontal(g2)
    c: Vertical(g1)
    c: DistanceX(g2) = -41
    c: DistanceX(g1) = 41
    c: DistanceY(g2) = -321
    c: Coincident(g3,g0)
    c: Coincident(g3,g2)
    c: Vertical(g3)
    c: DistanceY(g3,g3) = 72
    c: Equal(g4,g5)
    c: Equal(g4,g6)
    c: Equal(g4,g7)
    c: Diameter(g4) = 3.25
    c: DistanceY(g4,g5) = 0
    c: DistanceX(g7,g4) = 0
    c: DistanceX(g5,g6) = 0
    c: DistanceY(g7,g6) = 0
    c: DistanceX(g4) = -35
    c: DistanceY(g4) = -315
    c: DistanceX(g5) = 35
    c: DistanceY(g7) = -255
    c: DistanceX(g8) = -7.5
    c: DistanceY(g8) = -288.5
    c: DistanceX(g8,g8) = 0
    c: DistanceY(g8,g8) = 6.4
    c: Diameter(g8) = 10
    c: PointOnObject(g9,g-2)
    c: DistanceY(g9,g9) = 6.35
    c: DistanceX(g9,g9) = 0
    c: DistanceY(g9) = -288.5
    c: Coincident(g10,g9)
    c: Coincident(g10,g8)
    c: Coincident(g11,g9)
    c: Coincident(g11,g8)
    c: Diameter(g9) = 6.4
FEATURE [Part::Extrusion] Extrude030  label="base"
  Base = -> Sketch093
  Dir = (0,0,1)
  DirMode = 2
  FaceMakerClass = Part::FaceMakerBullseye
  LengthFwd = 4.5
  LengthRev = 0
  Placement = pos=(0,0,-313.5) rot=(0,0,1;0rad)
  Solid = true
  Symmetric = false
FEATURE [Part::MultiFuse] Fusion078  label="base011"
  Shapes = -> [Extrude030,Extrude005,Extrude004,Extrude003]
FEATURE [Sketcher::SketchObject] Sketch094
  FullyConstrained = true
  sketch-geometry (4):
    g0: ArcOfCircle CenterX=-7.5 CenterY=-288.5 CenterZ=0 NormalX=0 NormalY=0 NormalZ=1 AngleXU=0 Radius=5 StartAngle=1.5708 EndAngle=4.71239
    g1: ArcOfCircle CenterX=0 CenterY=-288.5 CenterZ=0 NormalX=0 NormalY=0 NormalZ=1 AngleXU=0 Radius=5 StartAngle=4.71239 EndAngle=7.85398
    g2: LineSegment StartX=-7.5 StartY=-293.5 StartZ=0 EndX=-9e-16 EndY=-293.5 EndZ=0
    g3: LineSegment StartX=1.5e-15 StartY=-283.5 StartZ=0 EndX=-7.5 EndY=-283.5 EndZ=0
  constraints (10):
    c: Tangent(g0,g2) = -1.5708
    c: Tangent(g2,g1) = -1.5708
    c: Tangent(g1,g3) = -1.5708
    c: Tangent(g3,g0) = -1.5708
    c: Equal(g0,g1)
    c: Horizontal(g2)
    c: DistanceX(g1) = 0
    c: Diameter(g1) = 10
    c: DistanceX(g0) = -7.5
    c: DistanceY(g0) = -288.5
FEATURE [Part::Extrusion] Extrude031  label="baseMicCut"
  Base = -> Sketch094
  Dir = (0,0,1)
  DirMode = 2
  FaceMakerClass = Part::FaceMakerBullseye
  LengthFwd = 5
  LengthRev = 0
  Placement = pos=(0,0,-309.75) rot=(0,0,1;0rad)
  Solid = true
  Symmetric = false
FEATURE [Part::Cut] Cut035  label="base012"
  Base = -> Fusion078
  Tool = -> Extrude031
FEATURE [Part::Cylinder] Cylinder092  label="base008"
  Angle = 360
  AttacherType = Attacher::AttachEngine3D
  FirstAngle = 0
  Height = 4.5
  Placement = pos=(136,0,65) rot=(0,0,1;0rad)
  Radius = 40
  SecondAngle = 0
FEATURE [Part::Cylinder] Cylinder093  label="baseCut001"
  Angle = 360
  AttacherType = Attacher::AttachEngine3D
  FirstAngle = 0
  Height = 7
  Placement = pos=(5,0,74) rot=(0,0,1;0rad)
  Radius = 24
  SecondAngle = 0
FEATURE [Part::Cylinder] Cylinder094
  Angle = 360
  AttacherType = Attacher::AttachEngine3D
  FirstAngle = 0
  Height = 14.5
  Placement = pos=(134,32.6,55) rot=(0,0,1;0rad)
  Radius = 5.5
  SecondAngle = 0
FEATURE [Part::Cylinder] Cylinder096
  Angle = 360
  AttacherType = Attacher::AttachEngine3D
  FirstAngle = 0
  Height = 5.82
  Placement = pos=(0,-21,0) rot=(0,0,1;0rad)
  Radius = 5
  SecondAngle = 0
FEATURE [Part::Cylinder] Cylinder097
  Angle = 360
  AttacherType = Attacher::AttachEngine3D
  FirstAngle = 0
  Height = 5.82
  Placement = pos=(20.5,-21,0) rot=(0,0,1;0rad)
  Radius = 5
  SecondAngle = 0
  expr: Radius = 5
FEATURE [Part::Cylinder] Cylinder098
  Angle = 360
  AttacherType = Attacher::AttachEngine3D
  FirstAngle = 0
  Height = 5.82
  Placement = pos=(0,-21,0) rot=(0,0,1;0rad)
  Radius = 5
  SecondAngle = 0
FEATURE [Part::Cylinder] Cylinder099
  Angle = 360
  AttacherType = Attacher::AttachEngine3D
  FirstAngle = 0
  Height = 5.82
  Placement = pos=(20.5,-21,0) rot=(0,0,1;0rad)
  Radius = 5
  SecondAngle = 0
FEATURE [Part::Cylinder] Cylinder100  label="m2HeatSetInsets004"
  Angle = 360
  AttacherType = Attacher::AttachEngine3D
  FirstAngle = 0
  Height = 10
  Placement = pos=(-30,0,65) rot=(0,0,1;0rad)
  Radius = 2
  SecondAngle = 0
  expr: Radius = 2
FEATURE [Part::Cylinder] Cylinder101  label="m2HeatSetInsets005"
  Angle = 360
  AttacherType = Attacher::AttachEngine3D
  FirstAngle = 0
  Height = 10
  Placement = pos=(40,0,65) rot=(0,0,1;0rad)
  Radius = 2
  SecondAngle = 0
FEATURE [Part::Cylinder] Cylinder102  label="m2HeatSetInsets006"
  Angle = 360
  AttacherType = Attacher::AttachEngine3D
  FirstAngle = 0
  Height = 10
  Placement = pos=(5,35,65) rot=(0,0,1;0rad)
  Radius = 2
  SecondAngle = 0
FEATURE [Part::Cylinder] Cylinder103  label="m2HeatSetInsets007"
  Angle = 360
  AttacherType = Attacher::AttachEngine3D
  FirstAngle = 0
  Height = 10
  Placement = pos=(5,-35,65) rot=(0,0,1;0rad)
  Radius = 2
  SecondAngle = 0
  expr: Radius = 2
FEATURE [Part::Cylinder] Cylinder104
  Angle = 360
  AttacherType = Attacher::AttachEngine3D
  FirstAngle = 0
  Height = 10
  Placement = pos=(0,-21,0) rot=(0,0,1;0rad)
  Radius = 2
  SecondAngle = 0
FEATURE [Part::Cylinder] Cylinder105
  Angle = 360
  AttacherType = Attacher::AttachEngine3D
  FirstAngle = 0
  Height = 10
  Placement = pos=(20.5,-21,0) rot=(0,0,1;0rad)
  Radius = 2
  SecondAngle = 0
FEATURE [Part::Cylinder] Cylinder106
  Angle = 360
  AttacherType = Attacher::AttachEngine3D
  FirstAngle = 0
  Height = 10
  Placement = pos=(0,-21,0) rot=(0,0,1;0rad)
  Radius = 2
  SecondAngle = 0
FEATURE [Part::Cylinder] Cylinder107
  Angle = 360
  AttacherType = Attacher::AttachEngine3D
  FirstAngle = 0
  Height = 10
  Placement = pos=(20.5,-21,0) rot=(0,0,1;0rad)
  Radius = 2
  SecondAngle = 0
FEATURE [Part::Cylinder] Cylinder110  label="WireCut001"
  Angle = 360
  AttacherType = Attacher::AttachEngine3D
  FirstAngle = 0
  Height = 60
  Placement = pos=(134,32.6,20) rot=(0,0,1;0rad)
  Radius = 2.5
  SecondAngle = 0
FEATURE [Part::Cylinder] Cylinder116  label="m2HeatSetInsets008"
  Angle = 360
  AttacherType = Attacher::AttachEngine3D
  FirstAngle = 0
  Height = 10
  Placement = pos=(-30,0,65) rot=(0,0,1;0rad)
  Radius = 2
  SecondAngle = 0
  expr: Radius = 2
FEATURE [Part::Cylinder] Cylinder117  label="m2HeatSetInsets009"
  Angle = 360
  AttacherType = Attacher::AttachEngine3D
  FirstAngle = 0
  Height = 10
  Placement = pos=(40,0,65) rot=(0,0,1;0rad)
  Radius = 2
  SecondAngle = 0
FEATURE [Part::Cylinder] Cylinder118  label="m2HeatSetInsets010"
  Angle = 360
  AttacherType = Attacher::AttachEngine3D
  FirstAngle = 0
  Height = 10
  Placement = pos=(5,35,65) rot=(0,0,1;0rad)
  Radius = 2
  SecondAngle = 0
FEATURE [Part::Cylinder] Cylinder119  label="m2HeatSetInsets011"
  Angle = 360
  AttacherType = Attacher::AttachEngine3D
  FirstAngle = 0
  Height = 10
  Placement = pos=(5,-35,65) rot=(0,0,1;0rad)
  Radius = 2
  SecondAngle = 0
  expr: Radius = 2
FEATURE [Part::Cylinder] Cylinder120
  Angle = 360
  AttacherType = Attacher::AttachEngine3D
  FirstAngle = 0
  Height = 10
  Placement = pos=(0,-21,0) rot=(0,0,1;0rad)
  Radius = 2
  SecondAngle = 0
FEATURE [Part::Cylinder] Cylinder121
  Angle = 360
  AttacherType = Attacher::AttachEngine3D
  FirstAngle = 0
  Height = 10
  Placement = pos=(20.5,-21,0) rot=(0,0,1;0rad)
  Radius = 2
  SecondAngle = 0
FEATURE [Part::Cylinder] Cylinder122
  Angle = 360
  AttacherType = Attacher::AttachEngine3D
  FirstAngle = 0
  Height = 10
  Placement = pos=(0,-21,0) rot=(0,0,1;0rad)
  Radius = 2
  SecondAngle = 0
FEATURE [Part::Cylinder] Cylinder123
  Angle = 360
  AttacherType = Attacher::AttachEngine3D
  FirstAngle = 0
  Height = 10
  Placement = pos=(20.5,-21,0) rot=(0,0,1;0rad)
  Radius = 2
  SecondAngle = 0
FEATURE [Part::Cylinder] Cylinder124  label="WireCut002"
  Angle = 360
  AttacherType = Attacher::AttachEngine3D
  FirstAngle = 0
  Height = 60
  Placement = pos=(134,32.6,20) rot=(0,0,1;0rad)
  Radius = 2.5
  SecondAngle = 0
FEATURE [Part::Cylinder] Cylinder125  label="lightin"
  Angle = 360
  AttacherType = Attacher::AttachEngine3D
  FirstAngle = 0
  Height = 21
  Placement = pos=(-129.35,-97.1,-100) rot=(1,0,0;0.698132rad)
  Radius = 5.25
  SecondAngle = 0
FEATURE [Part::Cylinder] Cylinder126
  Angle = 360
  AttacherType = Attacher::AttachEngine3D
  FirstAngle = 0
  Height = 10
  Placement = pos=(-129.35,-40.01,-39.84) rot=(1,0,0;0.698132rad)
  Radius = 2.75
  SecondAngle = 0
FEATURE [Part::Cylinder] Cylinder127
  Angle = 360
  AttacherType = Attacher::AttachEngine3D
  FirstAngle = 0
  Height = 21
  Placement = pos=(-129.35,-97.1,-100) rot=(1,0,0;0.698132rad)
  Radius = 2.25
  SecondAngle = 0
FEATURE [Part::MultiFuse] Fusion052  label="m3HeatSetCuts006"
  Placement = pos=(-5,39,70) rot=(0,0,1;0rad)
  Shapes = -> [Cylinder097,Cylinder096]
FEATURE [Part::MultiFuse] Fusion053  label="m3HeatSetCuts007"
  Placement = pos=(-5,3,70) rot=(0,0,1;0rad)
  Shapes = -> [Cylinder099,Cylinder098]
FEATURE [Part::MultiFuse] Fusion054  label="m3HeatSetCuts008"
  Placement = pos=(128.75,10,-1) rot=(0,0,1;0rad)
  Shapes = -> [Fusion053,Fusion052]
FEATURE [Part::MultiFuse] Fusion057
  Placement = pos=(129,10,0) rot=(0,0,1;0rad)
  Shapes = -> [Cylinder100,Cylinder101,Cylinder102,Cylinder103]
FEATURE [Part::MultiFuse] Fusion060  label="m3HeatSetCuts010"
  Placement = pos=(-5,39,70) rot=(0,0,1;0rad)
  Shapes = -> [Cylinder105,Cylinder104]
FEATURE [Part::MultiFuse] Fusion061  label="m3HeatSetCuts011"
  Placement = pos=(-5,3,70) rot=(0,0,1;0rad)
  Shapes = -> [Cylinder107,Cylinder106]
FEATURE [Part::MultiFuse] Fusion058  label="m3HeatSetCuts009"
  Placement = pos=(128.75,10,-1) rot=(0,0,1;0rad)
  Shapes = -> [Fusion061,Fusion060]
FEATURE [Part::MultiFuse] Fusion062  label="lightModuleCut"
  Shapes = -> [Fusion058,Fusion057,Cylinder110]
FEATURE [Part::MultiFuse] Fusion066
  Placement = pos=(129,10,0) rot=(0,0,1;0rad)
  Shapes = -> [Cylinder116,Cylinder117,Cylinder118,Cylinder119]
FEATURE [Part::MultiFuse] Fusion068  label="m3HeatSetCuts013"
  Placement = pos=(-5,39,70) rot=(0,0,1;0rad)
  Shapes = -> [Cylinder121,Cylinder120]
FEATURE [Part::MultiFuse] Fusion069  label="m3HeatSetCuts014"
  Placement = pos=(-5,3,70) rot=(0,0,1;0rad)
  Shapes = -> [Cylinder123,Cylinder122]
FEATURE [Part::MultiFuse] Fusion067  label="m3HeatSetCuts012"
  Placement = pos=(128.75,10,-1) rot=(0,0,1;0rad)
  Shapes = -> [Fusion069,Fusion068]
FEATURE [Part::MultiFuse] Fusion070  label="lightModuleCut001"
  Placement = pos=(-314,-122,-162) rot=(0,0,1;0rad)
  Shapes = -> [Fusion067,Fusion066,Cylinder124]
FEATURE [Part::MultiFuse] Fusion072  label="lightCuts"
  Shapes = -> [Cylinder127,Cylinder126]
FEATURE [Sketcher::SketchObject] Sketch061
  FullyConstrained = true
  Placement = pos=(0,0,0) rot=(0.57735,0.57735,0.57735;2.0944rad)
  sketch-geometry (4):
    g0: LineSegment StartX=-112 StartY=-91 StartZ=0 EndX=-108.786 EndY=-94.8302 EndZ=0
    g1: LineSegment StartX=-112 StartY=-91 StartZ=0 EndX=-39.9918 EndY=-30.578 EndZ=0
    g2: LineSegment StartX=-39.9918 StartY=-30.578 StartZ=0 EndX=-36.7779 EndY=-34.4082 EndZ=0
    g3: LineSegment StartX=-36.7779 StartY=-34.4082 StartZ=0 EndX=-108.786 EndY=-94.8302 EndZ=0
  constraints (12):
    c: Coincident(g1,g0)
    c: Coincident(g2,g1)
    c: Coincident(g3,g2)
    c: Coincident(g3,g0)
    c: DistanceX(g0) = -112
    c: Angle(g1) = 0.698132
    c: Parallel(g1,g3)
    c: Angle(g0,g1) = 1.5708
    c: Angle(g1,g2) = 1.5708
    c: Distance(g1) = 94
    c: Distance(g0,g0) = 5
    c: DistanceY(g0) = -91
FEATURE [Part::Extrusion] Extrude017  label="lightIn"
  Base = -> Sketch061
  Dir = (1,0,0)
  DirMode = 2
  FaceMakerClass = Part::FaceMakerBullseye
  LengthFwd = 15
  LengthRev = 0
  Placement = pos=(-138.75,0,0) rot=(0,0,1;0rad)
  Solid = true
  Symmetric = false
FEATURE [Sketcher::SketchObject] Sketch063
  FullyConstrained = false
  sketch-geometry (4):
    g0: LineSegment StartX=-180 StartY=-72 StartZ=0 EndX=-123.748 EndY=-72 EndZ=0
    g1: LineSegment StartX=-123.748 StartY=-72 StartZ=0 EndX=-123.748 EndY=-112 EndZ=0
    g2: LineSegment StartX=-123.748 StartY=-112 StartZ=0 EndX=-220 EndY=-112 EndZ=0
    g3: ArcOfCircle CenterX=-180 CenterY=-112 CenterZ=0 NormalX=0 NormalY=0 NormalZ=1 AngleXU=0 Radius=40 StartAngle=1.5708 EndAngle=3.14159
  constraints (12):
    c: Horizontal(g0)
    c: Coincident(g1,g0)
    c: Vertical(g1)
    c: Coincident(g2,g1)
    c: Horizontal(g2)
    c: PointOnObject(g3,g2)
    c: Coincident(g3,g0)
    c: Coincident(g2,g3)
    c: Radius(g3) = 40
    c: Angle(g3) = 1.5708
    c: DistanceX(g3) = -180
    c: DistanceY(g3) = -112
FEATURE [Part::Extrusion] Extrude019  label="lightModuleHold"
  Base = -> Sketch063
  Dir = (0,0,1)
  DirMode = 2
  FaceMakerClass = Part::FaceMakerBullseye
  LengthFwd = 4.5
  LengthRev = 0
  Placement = pos=(0,0,-97) rot=(0,0,1;0rad)
  Solid = true
  Symmetric = false
FEATURE [Sketcher::SketchObject] Sketch067
  FullyConstrained = true
  sketch-geometry (4):
    g0: LineSegment StartX=-138.75 StartY=-72 StartZ=0 EndX=-138.75 EndY=-80 EndZ=0
    g1: LineSegment StartX=-138.75 StartY=-80 StartZ=0 EndX=-123.75 EndY=-80 EndZ=0
    g2: LineSegment StartX=-123.75 StartY=-80 StartZ=0 EndX=-123.75 EndY=-72 EndZ=0
    g3: LineSegment StartX=-123.75 StartY=-72 StartZ=0 EndX=-138.75 EndY=-72 EndZ=0
  constraints (12):
    c: Vertical(g0)
    c: Coincident(g1,g0)
    c: Horizontal(g1)
    c: Coincident(g2,g1)
    c: Vertical(g2)
    c: Coincident(g3,g0)
    c: Horizontal(g3)
    c: DistanceY(g0) = -80
    c: DistanceY(g0,g0) = 8
    c: DistanceX(g0,g1) = 15
    c: DistanceX(g0) = -138.75
    c: Coincident(g2,g3)
FEATURE [Part::Extrusion] Extrude020  label="lightBaseSupport"
  Base = -> Sketch067
  Dir = (0,0,1)
  DirMode = 2
  FaceMakerClass = Part::FaceMakerBullseye
  LengthFwd = 33.5
  LengthRev = 0
  Placement = pos=(0,0,-97) rot=(0,0,1;0rad)
  Solid = true
  Symmetric = false
FEATURE [Sketcher::SketchObject] Sketch068
  FullyConstrained = true
  Placement = pos=(0,0,0) rot=(0.57735,0.57735,0.57735;2.0944rad)
  sketch-geometry (4):
    g0: LineSegment StartX=-112 StartY=-91 StartZ=0 EndX=-108.786 EndY=-94.8302 EndZ=0
    g1: LineSegment StartX=-112 StartY=-91 StartZ=0 EndX=-39.9918 EndY=-30.578 EndZ=0
    g2: LineSegment StartX=-39.9918 StartY=-30.578 StartZ=0 EndX=-36.7779 EndY=-34.4082 EndZ=0
    g3: LineSegment StartX=-36.7779 StartY=-34.4082 StartZ=0 EndX=-108.786 EndY=-94.8302 EndZ=0
  constraints (12):
    c: Coincident(g1,g0)
    c: Coincident(g2,g1)
    c: Coincident(g3,g2)
    c: Coincident(g3,g0)
    c: DistanceX(g0) = -112
    c: Angle(g1) = 0.698132
    c: Parallel(g1,g3)
    c: Angle(g0,g1) = 1.5708
    c: Angle(g1,g2) = 1.5708
    c: Distance(g1) = 94
    c: Distance(g0,g0) = 5
    c: DistanceY(g0) = -91
FEATURE [Part::Extrusion] Extrude021  label="lightModuleCut002"
  Base = -> Sketch068
  Dir = (1,0,0)
  DirMode = 2
  FaceMakerClass = Part::FaceMakerBullseye
  LengthFwd = 15
  LengthRev = 0
  Placement = pos=(-138.75,-7.78,0) rot=(0,0,1;0rad)
  Solid = true
  Symmetric = false
FEATURE [Part::MultiFuse] Fusion073
  Shapes = -> [Fusion072,Extrude021]
FEATURE [Part::MultiFuse] Fusion075  label="lightModuleCut003"
  Shapes = -> [Fusion070,Fusion073]
FEATURE [Sketcher::SketchObject] Sketch069
  FullyConstrained = true
  Placement = pos=(0,0,0) rot=(0.57735,0.57735,0.57735;2.0944rad)
  sketch-geometry (4):
    g0: LineSegment StartX=-112 StartY=-92.5 StartZ=0 EndX=-110.5 EndY=-92.5 EndZ=0
    g1: LineSegment StartX=-110.5 StartY=-92.5 StartZ=0 EndX=-110.5 EndY=-91 EndZ=0
    g2: LineSegment StartX=-110.5 StartY=-91 StartZ=0 EndX=-112 EndY=-91 EndZ=0
    g3: LineSegment StartX=-112 StartY=-91 StartZ=0 EndX=-112 EndY=-92.5 EndZ=0
  constraints (12):
    c: Coincident(g0,g1)
    c: Coincident(g1,g2)
    c: Coincident(g2,g3)
    c: Coincident(g3,g0)
    c: Horizontal(g0)
    c: Horizontal(g2)
    c: Vertical(g1)
    c: Vertical(g3)
    c: DistanceX(g0) = -112
    c: DistanceY(g0) = -92.5
    c: Distance(g3) = 1.5
    c: DistanceX(g0,g0) = 1.5
FEATURE [Part::Extrusion] Extrude022
  Base = -> Sketch069
  Dir = (1,0,0)
  DirMode = 2
  FaceMakerClass = Part::FaceMakerBullseye
  LengthFwd = 15
  LengthRev = 0
  Placement = pos=(-138.75,0,0) rot=(0,0,1;0rad)
  Solid = true
  Symmetric = false
FEATURE [Part::Sphere] Sphere003  label="SphereBase001"
  Angle1 = 0
  Angle2 = 12
  Angle3 = 360
  AttacherType = Attacher::AttachEngine3D
  Placement = pos=(5,0,74) rot=(0,0,1;0rad)
  Radius = 28.3
FEATURE [Part::Cut] Cut027
  Base = -> Sphere003
  Placement = pos=(131,0,-5) rot=(0,0,1;0rad)
  Tool = -> Cylinder093
FEATURE [Part::MultiFuse] Fusion055  label="Base001"
  Placement = pos=(-2,10,0) rot=(0,0,1;0rad)
  Shapes = -> [Cut027,Cylinder092]
FEATURE [Part::MultiFuse] Fusion056  label="lightModule002"
  Shapes = -> [Fusion055,Cylinder094,Fusion054]
FEATURE [Part::Cut] Cut028  label="lightModule003"
  Base = -> Fusion056
  Placement = pos=(-314,-122,-162) rot=(0,0,1;0rad)
  Tool = -> Fusion062
FEATURE [Part::MultiFuse] Fusion071  label="lightModuleHolder"
  Shapes = -> [Cut028,Extrude019]
FEATURE [Part::MultiFuse] Fusion074  label="lightModule004"
  Shapes = -> [Extrude017,Fusion071,Extrude020,Cylinder125]
FEATURE [Part::Cut] Cut030
  Base = -> Fusion074
  Tool = -> Fusion075
FEATURE [Part::MultiFuse] Fusion076  label="lightModule005"
  Shapes = -> [Cut030,Extrude022]
FEATURE [Part::Fillet] Fillet039
  Base = -> Fusion076
  Edges = 1 edges r=3: [Edge100]
FEATURE [Part::Fillet] Fillet040  label="lightModule006"
  Base = -> Fillet039
  Edges = 3 edges r=5: [Edge34,Edge94,Edge165]
FEATURE [Part::Cylinder] Cylinder128  label="base013"
  Angle = 360
  AttacherType = Attacher::AttachEngine3D
  FirstAngle = 0
  Height = 4.5
  Placement = pos=(136,0,65) rot=(0,0,1;0rad)
  Radius = 40
  SecondAngle = 0
FEATURE [Part::Cylinder] Cylinder129  label="baseCut002"
  Angle = 360
  AttacherType = Attacher::AttachEngine3D
  FirstAngle = 0
  Height = 7
  Placement = pos=(5,0,74) rot=(0,0,1;0rad)
  Radius = 24
  SecondAngle = 0
FEATURE [Part::Cylinder] Cylinder130
  Angle = 360
  AttacherType = Attacher::AttachEngine3D
  FirstAngle = 0
  Height = 1
  Placement = pos=(134,32.6,65) rot=(0,0,1;0rad)
  Radius = 5.5
  SecondAngle = 0
FEATURE [Part::Cylinder] Cylinder131
  Angle = 360
  AttacherType = Attacher::AttachEngine3D
  FirstAngle = 0
  Height = 5.82
  Placement = pos=(0,-21,0) rot=(0,0,1;0rad)
  Radius = 5
  SecondAngle = 0
FEATURE [Part::Cylinder] Cylinder132
  Angle = 360
  AttacherType = Attacher::AttachEngine3D
  FirstAngle = 0
  Height = 5.82
  Placement = pos=(20.5,-21,0) rot=(0,0,1;0rad)
  Radius = 5
  SecondAngle = 0
  expr: Radius = 5
FEATURE [Part::Cylinder] Cylinder133
  Angle = 360
  AttacherType = Attacher::AttachEngine3D
  FirstAngle = 0
  Height = 5.82
  Placement = pos=(0,-21,0) rot=(0,0,1;0rad)
  Radius = 5
  SecondAngle = 0
FEATURE [Part::Cylinder] Cylinder134
  Angle = 360
  AttacherType = Attacher::AttachEngine3D
  FirstAngle = 0
  Height = 5.82
  Placement = pos=(20.5,-21,0) rot=(0,0,1;0rad)
  Radius = 5
  SecondAngle = 0
FEATURE [Part::Cylinder] Cylinder135  label="m2HeatSetInsets012"
  Angle = 360
  AttacherType = Attacher::AttachEngine3D
  FirstAngle = 0
  Height = 10
  Placement = pos=(-30,0,65) rot=(0,0,1;0rad)
  Radius = 2
  SecondAngle = 0
  expr: Radius = 2
FEATURE [Part::Cylinder] Cylinder136  label="m2HeatSetInsets013"
  Angle = 360
  AttacherType = Attacher::AttachEngine3D
  FirstAngle = 0
  Height = 10
  Placement = pos=(40,0,65) rot=(0,0,1;0rad)
  Radius = 2
  SecondAngle = 0
FEATURE [Part::Cylinder] Cylinder137  label="m2HeatSetInsets014"
  Angle = 360
  AttacherType = Attacher::AttachEngine3D
  FirstAngle = 0
  Height = 10
  Placement = pos=(5,35,65) rot=(0,0,1;0rad)
  Radius = 2
  SecondAngle = 0
FEATURE [Part::Cylinder] Cylinder138  label="m2HeatSetInsets015"
  Angle = 360
  AttacherType = Attacher::AttachEngine3D
  FirstAngle = 0
  Height = 10
  Placement = pos=(5,-35,65) rot=(0,0,1;0rad)
  Radius = 2
  SecondAngle = 0
  expr: Radius = 2
FEATURE [Part::Cylinder] Cylinder139
  Angle = 360
  AttacherType = Attacher::AttachEngine3D
  FirstAngle = 0
  Height = 10
  Placement = pos=(0,-21,0) rot=(0,0,1;0rad)
  Radius = 2
  SecondAngle = 0
FEATURE [Part::Cylinder] Cylinder140
  Angle = 360
  AttacherType = Attacher::AttachEngine3D
  FirstAngle = 0
  Height = 10
  Placement = pos=(20.5,-21,0) rot=(0,0,1;0rad)
  Radius = 2
  SecondAngle = 0
FEATURE [Part::Cylinder] Cylinder141
  Angle = 360
  AttacherType = Attacher::AttachEngine3D
  FirstAngle = 0
  Height = 10
  Placement = pos=(0,-21,0) rot=(0,0,1;0rad)
  Radius = 2
  SecondAngle = 0
FEATURE [Part::Cylinder] Cylinder142
  Angle = 360
  AttacherType = Attacher::AttachEngine3D
  FirstAngle = 0
  Height = 10
  Placement = pos=(20.5,-21,0) rot=(0,0,1;0rad)
  Radius = 2
  SecondAngle = 0
FEATURE [Part::Cylinder] Cylinder143  label="WireCut003"
  Angle = 360
  AttacherType = Attacher::AttachEngine3D
  FirstAngle = 0
  Height = 60
  Placement = pos=(134,32.6,20) rot=(0,0,1;0rad)
  Radius = 2.5
  SecondAngle = 0
FEATURE [Part::MultiFuse] Fusion079  label="m3HeatSetCuts015"
  Placement = pos=(-5,39,70) rot=(0,0,1;0rad)
  Shapes = -> [Cylinder132,Cylinder131]
FEATURE [Part::MultiFuse] Fusion080  label="m3HeatSetCuts016"
  Placement = pos=(-5,3,70) rot=(0,0,1;0rad)
  Shapes = -> [Cylinder134,Cylinder133]
FEATURE [Part::MultiFuse] Fusion081  label="m3HeatSetCuts017"
  Placement = pos=(128.75,10,-1) rot=(0,0,1;0rad)
  Shapes = -> [Fusion080,Fusion079]
FEATURE [Part::MultiFuse] Fusion084
  Placement = pos=(129,10,0) rot=(0,0,1;0rad)
  Shapes = -> [Cylinder135,Cylinder136,Cylinder137,Cylinder138]
FEATURE [Part::MultiFuse] Fusion086  label="m3HeatSetCuts019"
  Placement = pos=(-5,39,70) rot=(0,0,1;0rad)
  Shapes = -> [Cylinder140,Cylinder139]
FEATURE [Part::MultiFuse] Fusion087  label="m3HeatSetCuts020"
  Placement = pos=(-5,3,70) rot=(0,0,1;0rad)
  Shapes = -> [Cylinder142,Cylinder141]
FEATURE [Part::MultiFuse] Fusion085  label="m3HeatSetCuts018"
  Placement = pos=(128.75,10,-1) rot=(0,0,1;0rad)
  Shapes = -> [Fusion087,Fusion086]
FEATURE [Part::MultiFuse] Fusion088  label="lightModuleCut004"
  Shapes = -> [Fusion085,Fusion084,Cylinder143]
FEATURE [Part::Sphere] Sphere004  label="SphereBase002"
  Angle1 = 0
  Angle2 = 12
  Angle3 = 360
  AttacherType = Attacher::AttachEngine3D
  Placement = pos=(5,0,74) rot=(0,0,1;0rad)
  Radius = 28.3
FEATURE [Part::Cut] Cut036
  Base = -> Sphere004
  Placement = pos=(131,0,-5) rot=(0,0,1;0rad)
  Tool = -> Cylinder129
FEATURE [Part::MultiFuse] Fusion082  label="Base002"
  Placement = pos=(-2,10,0) rot=(0,0,1;0rad)
  Shapes = -> [Cut036,Cylinder128]
FEATURE [Part::MultiFuse] Fusion083  label="lightModule008"
  Shapes = -> [Fusion082,Cylinder130,Fusion081]
FEATURE [Part::Cut] Cut037  label="lightModule007"
  Base = -> Fusion083
  Placement = pos=(-134,-360,-314) rot=(0,0,1;0rad)
  Tool = -> Fusion088
FEATURE [Part::Sphere] Sphere005  label="lightDome001"
  Angle1 = -90
  Angle2 = 90
  Angle3 = 180
  AttacherType = Attacher::AttachEngine3D
  Placement = pos=(0,-358,-245) rot=(1,0,0;1.5708rad)
  Radius = 30
FEATURE [Part::Cylinder] Cylinder144  label="base014"
  Angle = 360
  AttacherType = Attacher::AttachEngine3D
  FirstAngle = 0
  Height = 4.5
  Placement = pos=(136,0,65) rot=(0,0,1;0rad)
  Radius = 40
  SecondAngle = 0
FEATURE [Part::Cylinder] Cylinder145  label="baseCut003"
  Angle = 360
  AttacherType = Attacher::AttachEngine3D
  FirstAngle = 0
  Height = 7
  Placement = pos=(5,0,74) rot=(0,0,1;0rad)
  Radius = 24
  SecondAngle = 0
FEATURE [Part::Sphere] Sphere006  label="SphereBase003"
  Angle1 = 0
  Angle2 = 12
  Angle3 = 360
  AttacherType = Attacher::AttachEngine3D
  Placement = pos=(5,0,74) rot=(0,0,1;0rad)
  Radius = 28.3
FEATURE [Part::Cut] Cut038
  Base = -> Sphere006
  Placement = pos=(131,0,-5) rot=(0,0,1;0rad)
  Tool = -> Cylinder145
FEATURE [Part::MultiFuse] Fusion089  label="Base003"
  Placement = pos=(-129.5,10,-315.5) rot=(0,0,1;0rad)
  Shapes = -> [Cut038,Cylinder144]
FEATURE [Sketcher::SketchObject] Sketch095
  FullyConstrained = true
  sketch-geometry (4):
    g0: LineSegment StartX=-29.4 StartY=-303 StartZ=0 EndX=29.4 EndY=-303 EndZ=0
    g1: LineSegment StartX=29.4 StartY=-303 StartZ=0 EndX=39.5 EndY=-345 EndZ=0
    g2: LineSegment StartX=39.5 StartY=-345 StartZ=0 EndX=-39.5 EndY=-345 EndZ=0
    g3: LineSegment StartX=-39.5 StartY=-345 StartZ=0 EndX=-29.4 EndY=-303 EndZ=0
  constraints (12):
    c: Horizontal(g0)
    c: Coincident(g1,g0)
    c: Coincident(g2,g1)
    c: Horizontal(g2)
    c: Coincident(g3,g2)
    c: Coincident(g3,g0)
    c: DistanceX(g2) = -39.5
    c: DistanceY(g2) = -345
    c: DistanceX(g0) = -29.4
    c: DistanceX(g0) = 29.4
    c: DistanceX(g1) = 39.5
    c: DistanceY(g1,g0) = 42
FEATURE [Part::Extrusion] Extrude032  label="slsIn"
  Base = -> Sketch095
  Dir = (0,0,1)
  DirMode = 2
  FaceMakerClass = Part::FaceMakerBullseye
  LengthFwd = 4.5
  LengthRev = 0
  Placement = pos=(0,0,-249) rot=(0,0,1;0rad)
  Solid = true
  Symmetric = false
FEATURE [Sketcher::SketchObject] Sketch096
  FullyConstrained = true
  Placement = pos=(0,0,0) rot=(0.57735,0.57735,0.57735;2.0944rad)
  sketch-geometry (4):
    g0: LineSegment StartX=-358.25 StartY=-249 StartZ=0 EndX=-353.25 EndY=-249 EndZ=0
    g1: LineSegment StartX=-353.25 StartY=-249 StartZ=0 EndX=-326.489 EndY=-278.721 EndZ=0
    g2: LineSegment StartX=-326.489 StartY=-278.721 StartZ=0 EndX=-329.25 EndY=-281.208 EndZ=0
    g3: LineSegment StartX=-329.25 StartY=-281.208 StartZ=0 EndX=-358.25 EndY=-249 EndZ=0
  constraints (12):
    c: Coincident(g1,g0)
    c: Coincident(g0,g3)
    c: Horizontal(g0)
    c: DistanceX(g0,g0) = 5
    c: DistanceY(g0) = -249
    c: Coincident(g1,g2)
    c: Parallel(g3,g1)
    c: Coincident(g3,g2)
    c: Angle(g2,g3) = 1.5708
    c: Angle(g2) = -2.40855
    c: DistanceX(g3,g3) = 29
    c: DistanceX(g2) = -329.25
FEATURE [Part::Extrusion] Extrude033  label="slsIn001"
  Base = -> Sketch096
  Dir = (1,0,0)
  DirMode = 2
  FaceMakerClass = Part::FaceMakerBullseye
  LengthFwd = 20
  LengthRev = 0
  Placement = pos=(-10,0,0) rot=(0,0,1;0rad)
  Solid = true
  Symmetric = false
FEATURE [Part::Cylinder] Cylinder146
  Angle = 360
  AttacherType = Attacher::AttachEngine3D
  FirstAngle = 0
  Height = 23
  Placement = pos=(0,-318.74,-257.537) rot=(1,0,0;0.733038rad)
  Radius = 8
  SecondAngle = 0
FEATURE [Part::Cylinder] Cylinder147  label="cut"
  Angle = 360
  AttacherType = Attacher::AttachEngine3D
  FirstAngle = 0
  Height = 23
  Placement = pos=(0,-318.74,-257.537) rot=(1,0,0;0.733038rad)
  Radius = 4
  SecondAngle = 0
FEATURE [Part::Box] Box  label="Cube"
  AttacherType = Attacher::AttachEngine3D
  Height = 10
  Length = 24
  Placement = pos=(-12,-341.5,-244.5) rot=(0,0,1;0rad)
  Width = 23
FEATURE [Part::Cut] Cut039
  Base = -> Cylinder146
  Tool = -> Box
FEATURE [Part::MultiFuse] Fusion090
  Shapes = -> [Fusion043,Extrude032,Extrude033,Cut039]
FEATURE [Part::MultiFuse] Fusion091  label="sls015"
  Shapes = -> [Fusion090,Cut037]
FEATURE [Part::Cut] Cut040  label="sls016"
  Base = -> Fusion091
  Tool = -> Cylinder147
FEATURE [Mesh::Feature] SoLoNodesMay19_2022RainSensorHold
FEATURE [Mesh::Feature] SoLoNodesMay31_2023_baseSls  label="SoLoNodesMay31_2023-baseSls"
FEATURE [Mesh::Feature] SoLoNodesMay31_2023_sls018  label="SoLoNodesMay31_2023-sls018"
